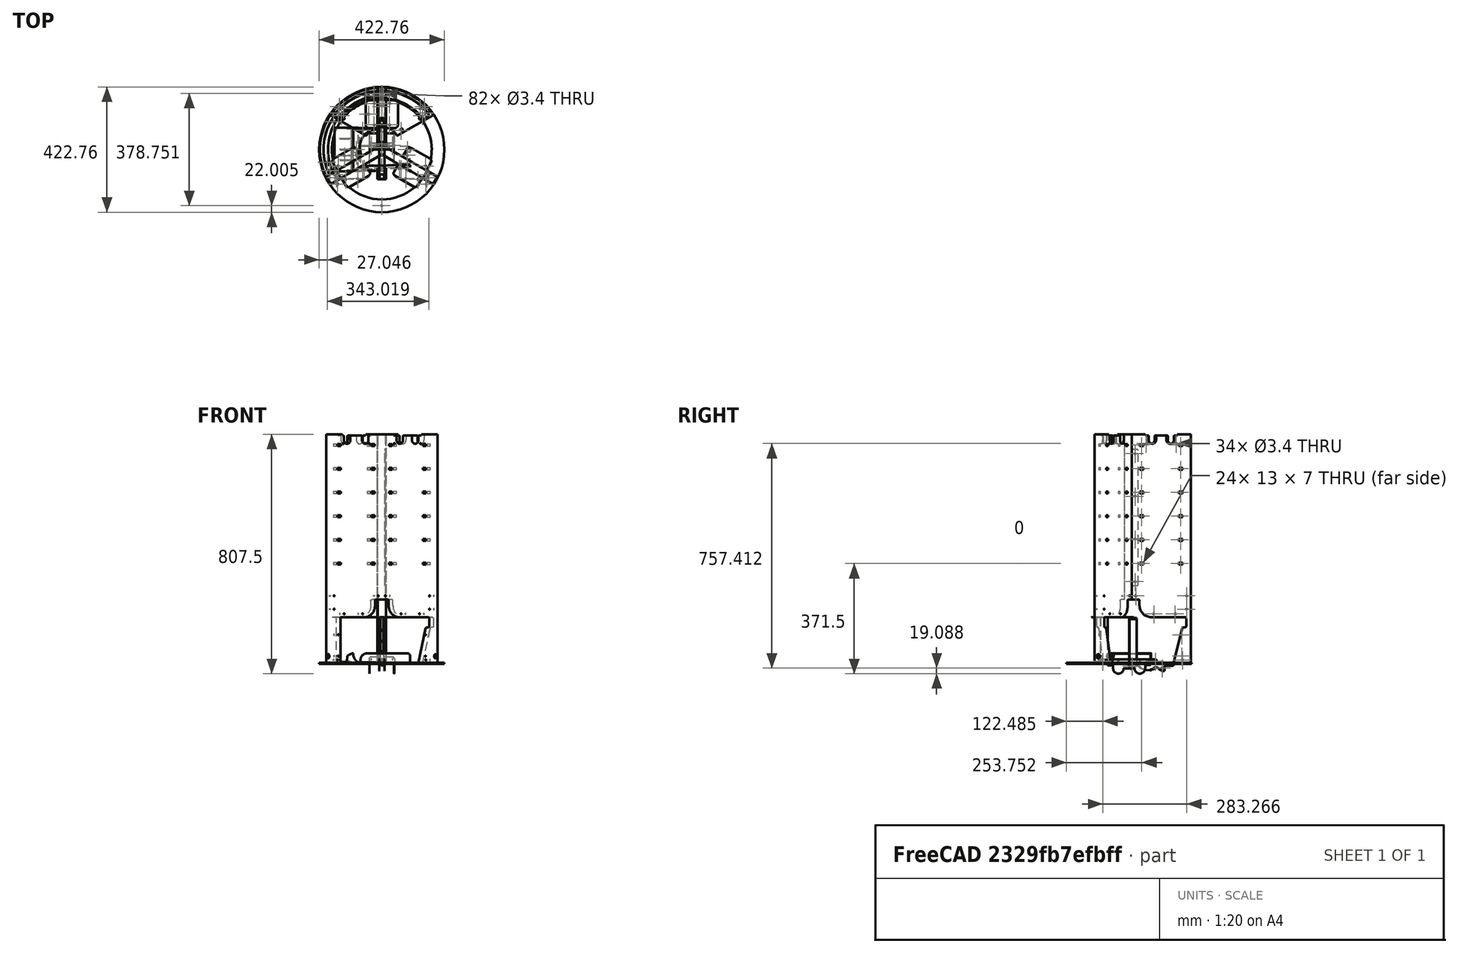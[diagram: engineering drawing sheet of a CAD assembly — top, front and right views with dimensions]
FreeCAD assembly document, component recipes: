
FREECAD ASSEMBLY — COMPONENT RECIPES ("composit_stand2_reserve")

This assembly document has 21 components, labeled P0..P20 below (a component is one placed body or linked part). 21 of them carry a construction recipe — the FreeCAD feature program that regenerates the part from scratch, quoted from this document or its linked companion documents; the rest are supplied as boundary geometry only. No exploded tour is included for this assembly.
NOTE — this tour is split across 2 documents so each fits a 32k-token context. This is document 1: the component sections continue in the remaining 1 document, each repeating the header above.
COMPONENT P0 — recipe-attached ("gutter001_material_0.50ansi", modeled in this document).
Construction recipe (the document's own serialized feature program — sketch geometry with constraints, then the solid features built on it; lengths are millimeters unless a unit is written):

FEATURE [Sketcher::SketchObject] Sketch  label="gutter_side_sketch"
  FullyConstrained = true
  MapMode = 5
  Support = -> [XY_Plane]
  sketch-geometry (15):
    g0: LineSegment StartX=0 StartY=150 StartZ=0 EndX=13.5 EndY=150 EndZ=0
    g1: LineSegment StartX=25.5 StartY=0 StartZ=0 EndX=0 EndY=0 EndZ=0
    g2: LineSegment StartX=15 StartY=148.5 StartZ=0 EndX=15 EndY=120 EndZ=0
    g3: LineSegment StartX=15 StartY=120 StartZ=0 EndX=29.7589 EndY=120 EndZ=0
    g4: GeomPoint X=25.5 Y=150 Z=0
    g5: ArcOfCircle CenterX=29.7589 CenterY=116.5 CenterZ=0 NormalX=0 NormalY=0 NormalZ=1 AngleXU=0 Radius=3.5 StartAngle=6.21662 EndAngle=7.85398
    g6: GeomPoint X=25.5 Y=0 Z=0
    g7: ArcOfCircle CenterX=13.5 CenterY=148.5 CenterZ=0 NormalX=0 NormalY=0 NormalZ=1 AngleXU=0 Radius=1.5 StartAngle=-2.7e-15 EndAngle=1.5708
    g8: GeomPoint X=15 Y=150 Z=0
    g9: LineSegment StartX=33.2511 StartY=116.267 StartZ=0 EndX=25.9178 EndY=6.26718 EndZ=0
    g10: LineSegment StartX=25.9178 StartY=6.26718 StartZ=0 EndX=25.5 EndY=0 EndZ=0
    g11: ArcOfCircle CenterX=22.4256 CenterY=6.5 CenterZ=0 NormalX=0 NormalY=0 NormalZ=1 AngleXU=0 Radius=3.5 StartAngle=4.71239 EndAngle=6.21662
    g12: LineSegment StartX=0 StartY=0 StartZ=0 EndX=0 EndY=3 EndZ=0
    g13: LineSegment StartX=0 StartY=3 StartZ=0 EndX=0 EndY=150 EndZ=0
    g14: LineSegment StartX=0 StartY=3 StartZ=0 EndX=22.4256 EndY=3 EndZ=0
  constraints (36):
    c: Coincident(g-1,g12)
    c: PointOnObject(g13,g-2)
    c: Coincident(g13,g0)
    c: Horizontal(g0)
    c: PointOnObject(g6,g-1)
    c: Coincident(g1,g12)
    c: Distance(g1,g6) = 25.5  'little_distance'
    c: Vertical(g2)
    c: Coincident(g3,g2)
    c: Horizontal(g3)
    c: DistanceY(g2,g8) = 30
    c: PointOnObject(g4,g0)
    c: Distance(g6,g4) = 150
    c: Distance(g0,g8) = 15
    c: Tangent(g3,g5) = 1.5708
    c: Diameter(g5) = 7
    c: PointOnObject(g8,g0)
    c: PointOnObject(g8,g2)
    c: Tangent(g0,g7) = 1.5708
    c: Tangent(g2,g7) = 1.5708
    c: Diameter(g7) = 3
    c: Tangent(g9,g5) = 1.5708
    c: Vertical(g4,g6)
    c: Coincident(g1,g6)
    c: Coincident(g10,g1)
    c: Coincident(g9,g10)
    c: Parallel(g9,g10)
    c: Angle(g10,g-1) = 1.63736
    c: Coincident(g12,g13)
    c: Vertical(g12)
    c: Coincident(g14,g12)
    c: Horizontal(g14)
    c: Tangent(g11,g9) = 1.5708
    c: Tangent(g14,g11) = -1.5708
    c: Equal(g11,g5)
    c: DistanceY(g12,g12) = 3
FEATURE [PartDesign::Pad] Pad  label="gutter_side_pad"
  Direction = (0,0,1)
  Length = 0.3
  Length2 = 10
  Profile = -> Sketch
  ReferenceAxis = -> Sketch [N_Axis]
  Type = 0
FEATURE [Sketcher::SketchObject] Sketch010
  FullyConstrained = true
  MapMode = 5
  Support = -> [XY_Plane]
  sketch-geometry (1):
    g0: LineSegment StartX=-8.49 StartY=0 StartZ=0 EndX=-8.49 EndY=150 EndZ=0
  constraints (4):
    c: PointOnObject(g0,g-1)
    c: Vertical(g0)
    c: DistanceX(g0) = -8.49
    c: DistanceY(g0) = 150
FEATURE [PartDesign::Mirrored] Mirrored005
  BaseFeature = -> Pad
  MirrorPlane = -> YZ_Plane
  Originals = -> [Pad]
  Refine = true
FEATURE [PartDesign::CoordinateSystem] Local_CS001
  AttacherType = Attacher::AttachEngine3D
  AttachmentOffset = pos=(-28.5,0,0) rot=(0,0,1;0.066568rad)
  MapMode = 5
  Placement = pos=(-28.5,0,0) rot=(0,0,1;0.066568rad)
  Support = -> [XY_Plane]
FEATURE [PartDesign::CoordinateSystem] Local_CS002
  AttacherType = Attacher::AttachEngine3D
  AttachmentOffset = pos=(28.5,0,0) rot=(0,0,1;-0.066568rad)
  MapMode = 5
  Placement = pos=(28.5,0,0) rot=(0,0,1;6.21662rad)
  Support = -> [XY_Plane]
FEATURE [PartDesign::CoordinateSystem] Local_CS003
  AttacherType = Attacher::AttachEngine3D
  AttachmentOffset = pos=(0,60,0) rot=(0,0,1;1.5708rad)
  MapMode = 5
  Placement = pos=(32.4911,59.8671,0) rot=(0,0,1;1.50423rad)
  Support = -> [Local_CS002]
FEATURE [PartDesign::CoordinateSystem] Local_CS004
  AttacherType = Attacher::AttachEngine3D
  AttachmentOffset = pos=(2,60,0) rot=(0,0,1;-1.5708rad)
  MapMode = 5
  Placement = pos=(-30.4956,60.0001,0) rot=(0,0,1;4.77896rad)
  Support = -> [Local_CS001]
FEATURE [PartDesign::Plane] DatumPlane003
  Length = 74.6163
  MapMode = 4
  Placement = pos=(32.4911,59.8671,0) rot=(0.023538,0.706911,0.706911;3.09453rad)
  ResizeMode = 0
  Support = -> [Local_CS003]
  Width = 61.2569
FEATURE [PartDesign::Plane] DatumPlane004
  Length = 72.6233
  MapMode = 4
  Placement = pos=(-30.4956,60.0001,0) rot=(0.998893,0.03326,0.03326;1.5719rad)
  ResizeMode = 0
  Support = -> [Local_CS004]
  Width = 61.0932
FEATURE [PartDesign::Plane] DatumPlane005
  AttachmentOffset = pos=(0,-1,0) rot=(0,0,1;0rad)
  Length = 199.341
  MapMode = 5
  Placement = pos=(33.4889,59.8006,0) rot=(0,0,1;1.50423rad)
  ResizeMode = 0
  Support = -> [Local_CS003]
  Width = 85.7622
FEATURE [PartDesign::Plane] DatumPlane006
  Length = 198.865
  MapMode = 5
  Placement = pos=(-30.4956,60.0001,0) rot=(0,0,-1;1.50423rad)
  ResizeMode = 0
  Support = -> [Local_CS004]
  Width = 82.4572
FEATURE [Sketcher::SketchObject] Sketch037
  AttachmentOffset = pos=(30,2,0) rot=(0,0,1;0rad)
  FullyConstrained = true
  MapMode = 5
  Placement = pos=(32.4911,89.9337,0) rot=(0,0,1;1.50423rad)
  Support = -> [Local_CS003]
  sketch-geometry (8):
    g0: LineSegment StartX=0 StartY=11.625 StartZ=0 EndX=1 EndY=11.625 EndZ=0
    g1: ArcOfCircle CenterX=1 CenterY=0 CenterZ=0 NormalX=0 NormalY=0 NormalZ=1 AngleXU=0 Radius=11.625 StartAngle=0.450911 EndAngle=1.5708
    g2: ArcOfCircle CenterX=17.127 CenterY=0 CenterZ=0 NormalX=0 NormalY=0 NormalZ=1 AngleXU=0 Radius=3 StartAngle=0.25268 EndAngle=1.29556
    g3: LineSegment StartX=12.0914 StartY=4.53943 StartZ=0 EndX=17.9423 EndY=2.88708 EndZ=0
    g4: LineSegment StartX=0 StartY=11.625 StartZ=0 EndX=0 EndY=0 EndZ=0
    g5: LineSegment StartX=0 StartY=0 StartZ=0 EndX=21 EndY=0 EndZ=0
    g6: ArcOfCircle CenterX=21 CenterY=1 CenterZ=0 NormalX=0 NormalY=0 NormalZ=1 AngleXU=0 Radius=1 StartAngle=3.39427 EndAngle=4.71239
    g7: ArcOfCircle CenterX=12.3631 CenterY=5.5018 CenterZ=0 NormalX=0 NormalY=0 NormalZ=1 AngleXU=0 Radius=1 StartAngle=3.5925 EndAngle=4.43715
  constraints (22):
    c: PointOnObject(g0,g-2)
    c: Horizontal(g0)
    c: PointOnObject(g2,g-1)
    c: Tangent(g3,g2) = 1.5708
    c: Tangent(g1,g0) = 1.5708
    c: Coincident(g4,g0)
    c: Coincident(g4,g-1)
    c: Coincident(g5,g4)
    c: Diameter(g2) = 6
    c: Angle(g3,g-1) = 0.275238
    c: Diameter(g1) = 23.25
    c: PointOnObject(g1,g-1)
    c: Distance(g0) = 1
    c: Horizontal(g5)
    c: Tangent(g6,g5) = -1.5708
    c: Tangent(g6,g2) = 1.5708
    c: Diameter(g6) = 2
    c: Distance(g5) = 21
    c: Tangent(g3,g7) = -1.5708
    c: Tangent(g1,g7) = 1.5708
    c: Diameter(g7) = 2
    c: DistanceY(g2) = 2.88708  'arc_height'
FEATURE [PartDesign::Pocket] Pocket008
  BaseFeature = -> Mirrored005
  Direction = (0,0,-1)
  Length = 5
  Length2 = 5
  Midplane = true
  Profile = -> Sketch037
  ReferenceAxis = -> Sketch037 [N_Axis]
  Type = 1
FEATURE [PartDesign::Mirrored] Mirrored006
  MirrorPlane = -> Sketch037 [V_Axis]
FEATURE [PartDesign::Mirrored] Mirrored007
  MirrorPlane = -> DatumPlane003
FEATURE [PartDesign::MultiTransform] MultiTransform002
  BaseFeature = -> Pocket008
  Originals = -> [Pocket008]
  Transformations = -> [Mirrored006,Mirrored007]
FEATURE [PartDesign::SubShapeBinder] Binder
  AttacherType = Attacher::AttachEngine3D
  AttachmentOffset = pos=(35,0,0) rot=(0,0,1;0rad)
  BindCopyOnChange = 0
  BindMode = 0
  ClaimChildren = true
  Context = -> Body [Binder.]
  Fuse = false
  MakeFace = true
  MapMode = 5
  OffsetFill = false
  OffsetIntersection = false
  OffsetJoinType = 0
  OffsetOpenResult = false
  PartialLoad = false
  Placement = pos=(-28.1674,25.0777,0) rot=(0,0,-1;1.50423rad)
  Relative = false
  _Version = 2
FEATURE [PartDesign::Pocket] Pocket009
  BaseFeature = -> MultiTransform002
  Direction = (0,0,-1)
  Length = 5
  Length2 = 5
  Midplane = true
  Profile = -> Binder
  Type = 1
FEATURE [PartDesign::Plane] DatumPlane007
  Length = 72.6233
  MapMode = 4
  Placement = pos=(-28.1674,25.0777,0) rot=(0.998893,0.03326,0.03326;1.5719rad)
  ResizeMode = 0
  Support = -> [Binder]
  Width = 61.0932
FEATURE [PartDesign::Mirrored] Mirrored008
  MirrorPlane = -> DatumPlane007
FEATURE [PartDesign::Mirrored] Mirrored009
  MirrorPlane = -> DatumPlane004
FEATURE [PartDesign::MultiTransform] MultiTransform003
  BaseFeature = -> Pocket009
  Originals = -> [Pocket009]
  Transformations = -> [Mirrored008,Mirrored009]
FEATURE [Sketcher::SketchObject] Sketch038
  FullyConstrained = true
  MapMode = 5
  Support = -> [XY_Plane]
  sketch-geometry (1):
    g0: LineSegment StartX=8.49 StartY=0 StartZ=0 EndX=8.49 EndY=150 EndZ=0
  constraints (4):
    c: PointOnObject(g0,g-1)
    c: Vertical(g0)
    c: DistanceX(g0) = 8.49
    c: DistanceY(g0) = 150
FEATURE [Sketcher::SketchObject] Sketch039
  AttachmentOffset = pos=(51,14,0) rot=(0,0,1;0rad)
  FullyConstrained = true
  MapMode = 5
  Placement = pos=(22.9124,111.619,0) rot=(0,0,1;1.50423rad)
  Support = -> [DatumPlane005]
  sketch-geometry (1):
    g0: Circle CenterX=0 CenterY=0 CenterZ=0 NormalX=0 NormalY=0 NormalZ=1 AngleXU=0 Radius=1.7
  constraints (2):
    c: Coincident(g0,g-1)
    c: Diameter(g0) = 3.4
FEATURE [PartDesign::Pocket] Pocket010
  BaseFeature = -> MultiTransform003
  Direction = (0,0,-1)
  Length = 5
  Length2 = 5
  Midplane = true
  Profile = -> Sketch039
  ReferenceAxis = -> Sketch039 [N_Axis]
  Type = 1
FEATURE [PartDesign::Mirrored] Mirrored010
  MirrorPlane = -> DatumPlane003
FEATURE [PartDesign::Mirrored] Mirrored011
  MirrorPlane = -> YZ_Plane
FEATURE [PartDesign::MultiTransform] MultiTransform004
  BaseFeature = -> Pocket010
  Originals = -> [Pocket010]
  Transformations = -> [Mirrored010,Mirrored011]
FEATURE [PartDesign::FeaturePython] Fold  # WARN: FeaturePython — macro-defined, semantics opaque (R4)
  BaseFeature = -> MultiTransform004
  BendLine = -> Sketch038
  Position = 0
  angle = 90
  baseObject = -> MultiTransform004 [Face4]
  invert = false
  invertbend = true
  kfactor = 0.01
  radius = 0.01
  unfold = false
FEATURE [PartDesign::FeaturePython] Fold002  # WARN: FeaturePython — macro-defined, semantics opaque (R4)
  BaseFeature = -> Fold
  BendLine = -> Sketch010
  Position = 0
  angle = 90
  baseObject = -> Fold [Face2]
  invert = false
  invertbend = false
  kfactor = 0.01
  radius = 0.01
  unfold = false
FEATURE [PartDesign::CoordinateSystem] Local_CS024
  AttacherType = Attacher::AttachEngine3D
  AttachmentOffset = pos=(0,60,-10.3215) rot=(-1,0,0;0.066568rad)
  MapMode = 5
  Placement = pos=(0,60,-10.3215) rot=(-1,0,0;0.066568rad)
  Support = -> [XY_Plane]
FEATURE [Sketcher::SketchObject] Sketch115
  FullyConstrained = true
  MapMode = 5
  Support = -> [XY_Plane]
  sketch-geometry (1):
    g0: Circle CenterX=0 CenterY=145 CenterZ=0 NormalX=0 NormalY=0 NormalZ=1 AngleXU=0 Radius=1.7
  constraints (3):
    c: PointOnObject(g0,g-2)
    c: Diameter(g0) = 3.4
    c: DistanceY(g0) = 145
FEATURE [PartDesign::Pocket] Pocket070
  BaseFeature = -> Fold002
  Direction = (0,0,-1)
  Length = 5
  Length2 = 5
  Midplane = true
  Profile = -> Sketch115
  ReferenceAxis = -> Sketch115 [N_Axis]
  Type = 1
FEATURE [PartDesign::Body] Body  label="gutter001_material_0.50ansi"
  Group = -> [Sketch,Pad,Mirrored005,Local_CS001,Local_CS002,Local_CS003,Local_CS004,DatumPlane003,DatumPlane004,DatumPlane005,DatumPlane006,Sketch037,Pocket008,MultiTransform002,Mirrored006,Mirrored007,Binder,Pocket009,MultiTransform003,Mirrored008,DatumPlane007,Mirrored009,Sketch010,Sketch038,Sketch039,Pocket010,MultiTransform004,Mirrored010,Mirrored011,Fold,Fold002,Local_CS024,Sketch115,Pocket070]
  Origin = -> Origin
  Tip = -> Pocket070
COMPONENT P1 — recipe-attached ("Body001_material_0.30ansi", modeled in this document).
Construction recipe (the document's own serialized feature program — sketch geometry with constraints, then the solid features built on it; lengths are millimeters unless a unit is written):

FEATURE [Sketcher::SketchObject] Sketch003
  FullyConstrained = true
  MapMode = 5
  Support = -> [XY_Plane001]
  sketch-geometry (12):
    g0: LineSegment StartX=-14.5 StartY=8.37158 StartZ=0 EndX=-14.5 EndY=208.372 EndZ=0
    g1: LineSegment StartX=-14.5 StartY=208.372 StartZ=0 EndX=14.5 EndY=208.372 EndZ=0
    g2: LineSegment StartX=14.5 StartY=208.372 StartZ=0 EndX=14.5 EndY=8.37158 EndZ=0
    g3: LineSegment StartX=14.5 StartY=8.37158 StartZ=0 EndX=187.705 EndY=-91.6284 EndZ=0
    g4: LineSegment StartX=187.705 StartY=-91.6284 StartZ=0 EndX=173.205 EndY=-116.743 EndZ=0
    g5: LineSegment StartX=173.205 StartY=-116.743 StartZ=0 EndX=0 EndY=-16.7432 EndZ=0
    g6: LineSegment StartX=0 StartY=-16.7432 StartZ=0 EndX=-173.205 EndY=-116.743 EndZ=0
    g7: LineSegment StartX=-173.205 StartY=-116.743 StartZ=0 EndX=-187.705 EndY=-91.6284 EndZ=0
    g8: LineSegment StartX=-187.705 StartY=-91.6284 StartZ=0 EndX=-14.5 EndY=8.37158 EndZ=0
    g9: LineSegment StartX=-14.5 StartY=8.37158 StartZ=0 EndX=0 EndY=0 EndZ=0
    g10: LineSegment StartX=0 StartY=0 StartZ=0 EndX=14.5 EndY=8.37158 EndZ=0
    g11: LineSegment StartX=0 StartY=0 StartZ=0 EndX=0 EndY=-16.7432 EndZ=0
  constraints (39):
    c: Vertical(g0)
    c: Coincident(g0,g1)
    c: Horizontal(g1)
    c: Coincident(g1,g2)
    c: Vertical(g2)
    c: Coincident(g2,g3)
    c: Coincident(g3,g4)
    c: Coincident(g4,g5)
    c: PointOnObject(g5,g-2)
    c: Coincident(g5,g6)
    c: Coincident(g6,g7)
    c: Coincident(g8,g7)
    c: Equal(g2,g6)
    c: Equal(g6,g5)
    c: Equal(g5,g3)
    c: Equal(g4,g7)
    c: Equal(g7,g1)
    c: Perpendicular(g4,g5)
    c: Perpendicular(g4,g3)
    c: Perpendicular(g7,g6)
    c: Perpendicular(g8,g7)
    c: Angle(g6,g5) = 2.0944
    c: Angle(g3,g2) = 2.0944
    c: Coincident(g9,g0)
    c: Coincident(g9,g-1)
    c: Coincident(g10,g9)
    c: Coincident(g10,g2)
    c: Coincident(g11,g9)
    c: Coincident(g11,g5)
    c: Equal(g10,g11)
    c: DistanceX(g1,g1) = 29
    c: DistanceY(g2,g2) = 200
    c: DistanceY(g9,g2) = 8.37158  'petal_offset'
    c: DistanceY(g0) = 8.37158  'petal_conn_y'
    c: Coincident(g8,g0)
    c: DistanceX(g2) = 14.5  'petal_conn_x'
    c: Distance(g9,g1) = 208.875  'max_r'
    c: Distance(g10) = 16.7432  'planes_intersec_r'
    c: DistanceY(g9,g1) = 208.372  'total_petal_length'
FEATURE [PartDesign::FeaturePython] BaseBend001  # WARN: FeaturePython — macro-defined, semantics opaque (R4)
  BendSide = 0
  BendSketch = -> Sketch003
  MidPlane = false
  Reverse = false
  length = 774
  radius = 0.01
  thickness = 0.3
FEATURE [PartDesign::CoordinateSystem] Local_CS
  AttacherType = Attacher::AttachEngine3D
  AttachmentOffset = pos=(0,8.37158,0) rot=(0,0,1;0rad)
  MapMode = 5
  Placement = pos=(0,8.37158,0) rot=(0,0,1;0rad)
  Support = -> [XY_Plane001]
FEATURE [PartDesign::Pocket] Pocket001
  BaseFeature = -> BaseBend001
  Direction = (0,0,-1)
  Length = 5
  Length2 = 5
  Midplane = true
  Profile = -> Sketch005
  ReferenceAxis = -> Sketch005 [N_Axis]
  Type = 1
FEATURE [PartDesign::FeaturePython] Bend009  # WARN: FeaturePython — macro-defined, semantics opaque (R4)
  AutoMiter = true
  BaseFeature = -> Pocket001
  BendType = 1
  LengthList = [203.464]
  LengthSpec = 0
  ReliefFactor = 0.7
  UseReliefFactor = false
  angle = 90
  baseObject = -> Pocket001 [Face61]
  bendAList = [90]
  extend1 = 0
  extend2 = 0
  gap1 = 0
  gap2 = 0
  invert = false
  kfactor = 0.5
  length = 203.464
  maxExtendDist = 5
  minGap = 0.1
  minReliefGap = 1
  miterangle1 = 0
  miterangle2 = 0
  offset = 0
  radius = 0.01
  reliefType = 0
  reliefd = 1
  reliefw = 0.8
  sketchflip = false
  sketchinvert = false
  unfold = false
FEATURE [PartDesign::FeaturePython] Bend010  # WARN: FeaturePython — macro-defined, semantics opaque (R4)
  AutoMiter = true
  BaseFeature = -> Bend009
  BendType = 0
  LengthList = [20]
  LengthSpec = 0
  ReliefFactor = 0.7
  UseReliefFactor = false
  angle = 60
  baseObject = -> Bend009 [Face3]
  bendAList = [60]
  extend1 = 0
  extend2 = 0
  gap1 = 0
  gap2 = 0
  invert = true
  kfactor = 0.5
  length = 20
  maxExtendDist = 5
  minGap = 0.1
  minReliefGap = 1
  miterangle1 = 0
  miterangle2 = 0
  offset = 0
  radius = 0.01
  reliefType = 0
  reliefd = 1
  reliefw = 0.8
  sketchflip = false
  sketchinvert = false
  unfold = false
FEATURE [PartDesign::CoordinateSystem] Local_CS011
  AttacherType = Attacher::AttachEngine3D
  AttachmentOffset = pos=(0,100,0) rot=(0,0,1;0rad)
  MapMode = 5
  Placement = pos=(0,108.372,0) rot=(0,0,1;0rad)
  Support = -> [Local_CS]
FEATURE [PartDesign::Plane] DatumPlane011
  AttachmentOffset = pos=(0,0,0) rot=(0,0,1;0.523599rad)
  Length = 589.355
  MapMode = 5
  Placement = pos=(0,0,0) rot=(0,0,1;0.523599rad)
  ResizeMode = 0
  Support = -> [XY_Plane001]
  Width = 574.61
FEATURE [PartDesign::CoordinateSystem] Local_CS035
  AttacherType = Attacher::AttachEngine3D
  AttachmentOffset = pos=(0,0,774) rot=(0,0,1;0rad)
  MapMode = 5
  Placement = pos=(0,108.372,774) rot=(0,0,1;0rad)
  Support = -> [Local_CS011]
FEATURE [PartDesign::CoordinateSystem] Local_CS036  label="droppers_center"
  AttacherType = Attacher::AttachEngine3D
  AttachmentOffset = pos=(0,0,-19) rot=(0,0,1;0rad)
  MapMode = 5
  Placement = pos=(0,108.372,755) rot=(0,0,1;0rad)
  Support = -> [Local_CS035]
FEATURE [PartDesign::CoordinateSystem] Local_CS037  label="gutter_fixture_center"
  AttacherType = Attacher::AttachEngine3D
  AttachmentOffset = pos=(0,0,-12) rot=(0,0,1;0rad)
  MapMode = 5
  Placement = pos=(0,108.372,743) rot=(0,0,1;0rad)
  Support = -> [Local_CS036]
FEATURE [PartDesign::CoordinateSystem] Local_CS038  label="modules_top_center"
  AttacherType = Attacher::AttachEngine3D
  AttachmentOffset = pos=(0,0,-5) rot=(0,0,1;0rad)
  MapMode = 5
  Placement = pos=(0,108.372,738) rot=(0,0,1;0rad)
  Support = -> [Local_CS037]
FEATURE [Sketcher::SketchObject] Sketch112
  FullyConstrained = true
  MapMode = 5
  Placement = pos=(0,0,0) rot=(0.57735,0.57735,0.57735;2.0944rad)
  Support = -> [YZ_Plane001]
  sketch-geometry (5):
    g0: LineSegment StartX=-6.5 StartY=-3.5 StartZ=0 EndX=-6.5 EndY=3.5 EndZ=0
    g1: LineSegment StartX=-6.5 StartY=3.5 StartZ=0 EndX=6.5 EndY=3.5 EndZ=0
    g2: LineSegment StartX=6.5 StartY=3.5 StartZ=0 EndX=6.5 EndY=-3.5 EndZ=0
    g3: LineSegment StartX=6.5 StartY=-3.5 StartZ=0 EndX=-6.5 EndY=-3.5 EndZ=0
    g4: GeomPoint X=0 Y=0 Z=0
  constraints (12):
    c: Coincident(g0,g1)
    c: Coincident(g1,g2)
    c: Coincident(g2,g3)
    c: Coincident(g3,g0)
    c: Horizontal(g1)
    c: Horizontal(g3)
    c: Vertical(g0)
    c: Vertical(g2)
    c: Symmetric(g1,g0,g4)
    c: Coincident(g4,g-1)
    c: DistanceX(g1,g1) = 13
    c: DistanceY(g2,g2) = 7
FEATURE [Sketcher::SketchObject] Sketch113
  FullyConstrained = true
  MapMode = 5
  Placement = pos=(0,0,0) rot=(0.57735,0.57735,0.57735;2.0944rad)
  Support = -> [YZ_Plane001]
  sketch-geometry (8):
    g0: ArcOfCircle CenterX=0 CenterY=0 CenterZ=0 NormalX=0 NormalY=0 NormalZ=1 AngleXU=0 Radius=12.625 StartAngle=3.14159 EndAngle=6.28319
    g1: LineSegment StartX=12.625 StartY=-3.1e-15 StartZ=0 EndX=12.625 EndY=12.5 EndZ=0
    g2: LineSegment StartX=-12.625 StartY=1.5e-15 StartZ=0 EndX=-12.625 EndY=12.5 EndZ=0
    g3: ArcOfCircle CenterX=15.125 CenterY=12.5 CenterZ=0 NormalX=0 NormalY=0 NormalZ=1 AngleXU=0 Radius=2.5 StartAngle=1.5708 EndAngle=3.14159
    g4: ArcOfCircle CenterX=-15.125 CenterY=12.5 CenterZ=0 NormalX=0 NormalY=0 NormalZ=1 AngleXU=0 Radius=2.5 StartAngle=0 EndAngle=1.5708
    g5: LineSegment StartX=-15.125 StartY=15 StartZ=0 EndX=-15.125 EndY=19 EndZ=0
    g6: LineSegment StartX=-15.125 StartY=19 StartZ=0 EndX=15.125 EndY=19 EndZ=0
    g7: LineSegment StartX=15.125 StartY=19 StartZ=0 EndX=15.125 EndY=15 EndZ=0
  constraints (24):
    c: Coincident(g0,g-1)
    c: PointOnObject(g0,g-1)
    c: PointOnObject(g0,g-1)
    c: Coincident(g1,g0)
    c: Vertical(g1)
    c: Coincident(g2,g0)
    c: Vertical(g2)
    c: Coincident(g5,g4)
    c: Vertical(g5)
    c: Coincident(g6,g5)
    c: Horizontal(g6)
    c: Coincident(g7,g6)
    c: Coincident(g7,g3)
    c: Vertical(g7)
    c: Perpendicular(g3,g7)
    c: Tangent(g3,g1) = 1.5708
    c: Tangent(g4,g2) = -1.5708
    c: Perpendicular(g4,g5)
    c: Diameter(g0) = 25.25
    c: Distance(g0,g6) = 19
    c: Equal(g4,g3)
    c: Diameter(g4) = 5
    c: DistanceY(g7,g7) = 4
    c: Equal(g5,g7)
FEATURE [PartDesign::CoordinateSystem] Local_CS039
  AttacherType = Attacher::AttachEngine3D
  AttachmentOffset = pos=(119.5,154,11.5) rot=(0,0.707107,0.707107;3.14159rad)
  MapMode = 5
  Placement = pos=(11.5,119.5,154) rot=(0,0,1;4.71239rad)
  Support = -> [YZ_Plane001]
FEATURE [Sketcher::SketchObject] Sketch128
  FullyConstrained = true
  MapMode = 5
  Placement = pos=(0,0,0) rot=(0.57735,0.57735,0.57735;2.0944rad)
  Support = -> [YZ_Plane001]
  sketch-geometry (4):
    g0: LineSegment StartX=73 StartY=116.5 StartZ=0 EndX=166 EndY=116.5 EndZ=0
    g1: LineSegment StartX=166 StartY=116.5 StartZ=0 EndX=166 EndY=157 EndZ=0
    g2: LineSegment StartX=166 StartY=157 StartZ=0 EndX=73 EndY=157 EndZ=0
    g3: LineSegment StartX=73 StartY=157 StartZ=0 EndX=73 EndY=116.5 EndZ=0
  constraints (12):
    c: Coincident(g0,g1)
    c: Coincident(g1,g2)
    c: Coincident(g2,g3)
    c: Coincident(g3,g0)
    c: Horizontal(g0)
    c: Horizontal(g2)
    c: Vertical(g1)
    c: Vertical(g3)
    c: DistanceX(g0,g0) = 93  'length'
    c: DistanceY(g3,g3) = 40.5  'height'
    c: DistanceX(g0) = 73  'offset_x'
    c: DistanceY(g2) = 157
FEATURE [PartDesign::Pocket] Pocket081
  BaseFeature = -> Bend010
  Direction = (-1,2e-16,-3e-16)
  Length = 5
  Length2 = 5
  Midplane = true
  Profile = -> Sketch128
  ReferenceAxis = -> Sketch128 [N_Axis]
  Type = 1
FEATURE [PartDesign::PolarPattern] PolarPattern016
  Angle = 360
  Axis = -> Z_Axis001
  BaseFeature = -> Pocket081
  Occurrences = 3
  Originals = -> [Pocket081]
FEATURE [PartDesign::FeaturePython] Bend  # WARN: FeaturePython — macro-defined, semantics opaque (R4)
  AutoMiter = true
  BaseFeature = -> PolarPattern016
  BendType = 0
  LengthList = [40]
  LengthSpec = 2
  ReliefFactor = 0.7
  UseReliefFactor = false
  angle = 90
  baseObject = -> PolarPattern016 [Edge222,Edge178,Edge34,Edge78,Edge106,Edge150]
  bendAList = [90]
  extend1 = 0
  extend2 = 0
  gap1 = 0.1
  gap2 = 0.1
  invert = false
  kfactor = 0.5
  length = 40
  maxExtendDist = 5
  minGap = 0.1
  minReliefGap = 1
  miterangle1 = 0
  miterangle2 = 0
  offset = 0
  radius = 0.1
  reliefType = 0
  reliefd = 1
  reliefw = 0.8
  sketchflip = false
  sketchinvert = false
  unfold = false
FEATURE [Sketcher::SketchObject] Sketch129
  AttachmentOffset = pos=(0,0,0) rot=(0,1,0;3.66519rad)
  FullyConstrained = true
  MapMode = 5
  Placement = pos=(0,0,0) rot=(-0.186157,0.694747,0.694747;3.50969rad)
  Support = -> [XZ_Plane001]
  sketch-geometry (9):
    g0: LineSegment StartX=0 StartY=0 StartZ=0 EndX=169.18 EndY=0 EndZ=0
    g1: LineSegment StartX=169.18 StartY=0 StartZ=0 EndX=169.18 EndY=157 EndZ=0
    g2: LineSegment StartX=0 StartY=157 StartZ=0 EndX=0 EndY=0 EndZ=0
    g3: LineSegment StartX=73 StartY=116.5 StartZ=0 EndX=166 EndY=116.5 EndZ=0
    g4: LineSegment StartX=166 StartY=116.5 StartZ=0 EndX=166 EndY=157 EndZ=0
    g5: LineSegment StartX=166 StartY=157 StartZ=0 EndX=73 EndY=157 EndZ=0
    g6: LineSegment StartX=73 StartY=157 StartZ=0 EndX=73 EndY=116.5 EndZ=0
    g7: LineSegment StartX=169.18 StartY=157 StartZ=0 EndX=166 EndY=157 EndZ=0
    g8: LineSegment StartX=73 StartY=157 StartZ=0 EndX=0 EndY=157 EndZ=0
  constraints (25):
    c: Coincident(g0,g1)
    c: Coincident(g1,g7)
    c: Coincident(g8,g2)
    c: Coincident(g2,g0)
    c: Horizontal(g0)
    c: Vertical(g1)
    c: Vertical(g2)
    c: Coincident(g0,g-1)
    c: DistanceY(g8) = 157
    c: Coincident(g3,g4)
    c: Coincident(g4,g5)
    c: Coincident(g5,g6)
    c: Coincident(g6,g3)
    c: Horizontal(g3)
    c: Horizontal(g5)
    c: Vertical(g4)
    c: Vertical(g6)
    c: DistanceX(g3,g3) = 93  'length'
    c: DistanceY(g6,g6) = 40.5  'height'
    c: DistanceX(g3) = 73
    c: DistanceY(g5) = 157
    c: Horizontal(g7)
    c: Coincident(g8,g5)
    c: Coincident(g7,g4)
    c: DistanceX(g7,g7) = 3.18
FEATURE [PartDesign::CoordinateSystem] Local_CS041
  AttacherType = Attacher::AttachEngine3D
  AttachmentOffset = pos=(119.5,157,14.5) rot=(0,0.707107,0.707107;3.14159rad)
  MapMode = 5
  Placement = pos=(14.5,119.5,157) rot=(0,0,1;4.71239rad)
  Support = -> [YZ_Plane001]
FEATURE [Sketcher::SketchObject] Sketch130
  AttachmentOffset = pos=(0,40,0) rot=(0,0,1;0rad)
  FullyConstrained = true
  MapMode = 5
  Placement = pos=(54.5,119.5,157) rot=(0,0,-1;1.5708rad)
  Support = -> [Local_CS041]
  sketch-geometry (6):
    g0: ArcOfCircle CenterX=36.5 CenterY=-10 CenterZ=0 NormalX=0 NormalY=0 NormalZ=1 AngleXU=0 Radius=10 StartAngle=6.28318 EndAngle=7.85398
    g1: ArcOfCircle CenterX=-36.5 CenterY=-10 CenterZ=0 NormalX=0 NormalY=0 NormalZ=1 AngleXU=0 Radius=10 StartAngle=1.5708 EndAngle=3.14159
    g2: LineSegment StartX=-46.5 StartY=-10 StartZ=0 EndX=-46.5 EndY=0 EndZ=0
    g3: LineSegment StartX=-36.5 StartY=0 StartZ=0 EndX=-46.5 EndY=0 EndZ=0
    g4: LineSegment StartX=46.5 StartY=-10 StartZ=0 EndX=46.5 EndY=0 EndZ=0
    g5: LineSegment StartX=36.5 StartY=0 StartZ=0 EndX=46.5 EndY=0 EndZ=0
  constraints (17):
    c: PointOnObject(g0,g-1)
    c: PointOnObject(g1,g-1)
    c: Coincident(g2,g1)
    c: PointOnObject(g2,g-1)
    c: Vertical(g2)
    c: Tangent(g2,g1)
    c: Coincident(g3,g2)
    c: Coincident(g4,g0)
    c: PointOnObject(g4,g-1)
    c: Vertical(g4)
    c: Tangent(g4,g0)
    c: Coincident(g5,g4)
    c: Tangent(g5,g0) = 1.5708
    c: Tangent(g3,g1) = -1.5708
    c: DistanceX(g2,g4) = 93
    c: Symmetric(g1,g0,g-2)
    c: Diameter(g0) = 20
FEATURE [PartDesign::Pocket] Pocket083
  BaseFeature = -> Bend
  Direction = (0,-3e-16,-1)
  Length = 5
  Length2 = 5
  Midplane = true
  Profile = -> Sketch130
  ReferenceAxis = -> Sketch130 [N_Axis]
  Type = 1
FEATURE [PartDesign::Mirrored] Mirrored040
  MirrorPlane = -> YZ_Plane001
FEATURE [PartDesign::PolarPattern] PolarPattern017
  Angle = 360
  Axis = -> Z_Axis001
  Occurrences = 3
FEATURE [PartDesign::MultiTransform] MultiTransform014
  BaseFeature = -> Pocket083
  Originals = -> [Pocket083]
  Transformations = -> [Mirrored040,PolarPattern017]
FEATURE [PartDesign::Pocket] Pocket082
  BaseFeature = -> MultiTransform014
  Direction = (0.5,-0.866025,-1e-16)
  Length = 30
  Length2 = 5
  Midplane = true
  Profile = -> Sketch129
  ReferenceAxis = -> Sketch129 [N_Axis]
  Type = 0
FEATURE [PartDesign::Pocket] Pocket006
  BaseFeature = -> Pocket082
  Direction = (-1,2e-16,-3e-16)
  Length = 30
  Length2 = 160
  Midplane = true
  Profile = -> Sketch009
  ReferenceAxis = -> Sketch009 [N_Axis]
  Type = 0
FEATURE [PartDesign::Mirrored] Mirrored002
  BaseFeature = -> Pocket006
  MirrorPlane = -> DatumPlane014
  Originals = -> [Pocket006]
FEATURE [PartDesign::Pocket] Pocket014
  BaseFeature = -> Mirrored002
  Direction = (-1,2e-16,-3e-16)
  Length = 5
  Length2 = 5
  Midplane = true
  Profile = -> Sketch013
  ReferenceAxis = -> Sketch013 [N_Axis]
  Type = 1
FEATURE [PartDesign::PolarPattern] PolarPattern003
  Angle = 360
  Axis = -> Z_Axis001
  BaseFeature = -> Pocket014
  Occurrences = 3
  Originals = -> [Pocket014]
  Refine = true
FEATURE [PartDesign::Pocket] Pocket007
  BaseFeature = -> PolarPattern003
  Direction = (-1,2e-16,-3e-16)
  Length = 11.5
  Length2 = 5
  Profile = -> Sketch012
  ReferenceAxis = -> Sketch012 [N_Axis]
  Reversed = true
  Type = 0
FEATURE [PartDesign::CoordinateSystem] Local_CS042
  AttacherType = Attacher::AttachEngine3D
  AttachmentOffset = pos=(0,0,0) rot=(0,0,1;2.0944rad)
  MapMode = 5
  Placement = pos=(0,0,0) rot=(0,0,1;2.0944rad)
  Support = -> [XY_Plane001]
FEATURE [PartDesign::CoordinateSystem] Local_CS012
  AttacherType = Attacher::AttachEngine3D
  AttachmentOffset = pos=(14.5,119.5,157) rot=(0,0,1;4.71239rad)
  MapMode = 5
  Placement = pos=(-110.74,-47.1926,157) rot=(0,0,-1;5.75959rad)
  Support = -> [Local_CS042]
FEATURE [PartDesign::Plane] DatumPlane012
  Length = 589.355
  MapMode = 5
  Placement = pos=(-110.74,-47.1926,157) rot=(0,0,1;0.523599rad)
  ResizeMode = 0
  Support = -> [Local_CS012]
  Width = 574.61
FEATURE [PartDesign::Body] Body001  label="Body001_material_0.30ansi"
  Group = -> [Local_CS,Local_CS011,Sketch003,BaseBend001,Local_CS012,DatumPlane011,DatumPlane012,Local_CS035,Local_CS036,Local_CS037,Local_CS038,Sketch112,Sketch113,Pocket001,Bend009,Bend010,Sketch128,Pocket081,Local_CS039,PolarPattern016,Bend,Sketch129,Local_CS041,Sketch130,Pocket083,MultiTransform014,Mirrored040,PolarPattern017,Local_CS042,Pocket082,Pocket006,Mirrored002,Pocket014,PolarPattern003,Pocket007,+64 more]
  Origin = -> Origin001
  Tip = -> MultiTransform012
COMPONENT P2 — recipe-attached ("module001", modeled in this document).
Construction recipe (the document's own serialized feature program — sketch geometry with constraints, then the solid features built on it; lengths are millimeters unless a unit is written):

FEATURE [PartDesign::FeatureBase] BaseFeature
  BaseFeature = -> Part__Feature
FEATURE [PartDesign::CoordinateSystem] Local_CS009
  AttacherType = Attacher::AttachEngine3D
  MapMode = 45
  Placement = pos=(0,0,0) rot=(0,0.707107,0.707107;3.14159rad)
  Support = -> [BaseFeature]
FEATURE [PartDesign::Body] Body001003  label="module001"
  BaseFeature = -> Part__Feature
  Group = -> [BaseFeature,Local_CS009]
  Origin = -> Origin013
  Tip = -> BaseFeature
COMPONENT P3 — recipe-attached ("basin_cover", modeled in this document).
Construction recipe (the document's own serialized feature program — sketch geometry with constraints, then the solid features built on it; lengths are millimeters unless a unit is written):

FEATURE [Sketcher::SketchObject] Sketch047
  FullyConstrained = true
  MapMode = 5
  Support = -> [XY_Plane015]
  sketch-geometry (8):
    g0: ArcOfCircle CenterX=0 CenterY=16.7432 CenterZ=0 NormalX=0 NormalY=0 NormalZ=1 AngleXU=0 Radius=60 StartAngle=0.539993 EndAngle=1.5708
    g1: ArcOfCircle CenterX=52.3205 CenterY=48.1051 CenterZ=0 NormalX=0 NormalY=0 NormalZ=1 AngleXU=0 Radius=1 StartAngle=3.68159 EndAngle=5.23599
    g2: LineSegment StartX=52.8205 StartY=47.2391 StartZ=0 EndX=172.274 EndY=116.206 EndZ=0
    g3: ArcOfCircle CenterX=171.774 CenterY=117.072 CenterZ=0 NormalX=0 NormalY=0 NormalZ=1 AngleXU=0 Radius=1 StartAngle=5.23599 EndAngle=6.88142
    g4: ArcOfCircle CenterX=0 CenterY=0 CenterZ=0 NormalX=0 NormalY=0 NormalZ=1 AngleXU=0 Radius=208.875 StartAngle=0.598232 EndAngle=1.5708
    g5: LineSegment StartX=3.7e-15 StartY=76.7432 StartZ=0 EndX=1.28e-14 EndY=208.875 EndZ=0
    g6: LineSegment StartX=52.8205 StartY=47.2391 StartZ=0 EndX=0 EndY=16.7432 EndZ=0
    g7: GeomPoint X=173.205 Y=116.743 Z=0
  constraints (22):
    c: PointOnObject(g0,g-2)
    c: PointOnObject(g4,g-2)
    c: Diameter(g1) = 2
    c: Diameter(g3) = 2
    c: Tangent(g1,g0) = 1.5708
    c: Tangent(g3,g2) = -1.5708
    c: Angle(g2,g-1) = 2.61799
    c: Coincident(g5,g0)
    c: Coincident(g5,g4)
    c: Tangent(g1,g2) = -1.5708
    c: Coincident(g6,g1)
    c: Tangent(g6,g2)
    c: Coincident(g6,g0)
    c: Diameter(g0) = 120
    c: PointOnObject(g7,g4)
    c: PointOnObject(g7,g2)
    c: DistanceY(g4) = 208.875
    c: Distance(g4,g0) = 16.7432  'major_r_offset'
    c: Coincident(g4,g-1)
    c: PointOnObject(g0,g-2)
    c: Distance(g0,g7) = 200
    c: Tangent(g3,g4) = -1.5708
FEATURE [PartDesign::Pad] Pad012
  Direction = (0,0,1)
  Length = 3
  Length2 = 10
  Profile = -> Sketch047
  ReferenceAxis = -> Sketch047 [N_Axis]
  Type = 0
FEATURE [PartDesign::CoordinateSystem] Local_CS013
  AttacherType = Attacher::AttachEngine3D
  MapMode = 5
  Support = -> [XY_Plane015]
FEATURE [PartDesign::CoordinateSystem] Local_CS016
  AttacherType = Attacher::AttachEngine3D
  AttachmentOffset = pos=(0,0,0) rot=(0,0,1;0.523599rad)
  MapMode = 5
  Placement = pos=(0,0,0) rot=(0,0,1;0.523599rad)
  Support = -> [XY_Plane015]
FEATURE [PartDesign::Plane] DatumPlane015
  Length = 81.9615
  MapMode = 5
  Placement = pos=(0,0,0) rot=(0,0,1;0.523599rad)
  ResizeMode = 0
  Support = -> [Local_CS016]
  Width = 81.9615
FEATURE [PartDesign::Plane] DatumPlane016
  Length = 79.989
  MapMode = 4
  Placement = pos=(86.82,84.1932,0) rot=(0.377964,0.654654,0.654654;2.41886rad)
  ResizeMode = 0
  Width = 61.6877
FEATURE [PartDesign::CoordinateSystem] Local_CS026
  AttacherType = Attacher::AttachEngine3D
  AttachmentOffset = pos=(0,16.7432,0) rot=(0,0,1;0.523599rad)
  MapMode = 5
  Placement = pos=(0,16.7432,0) rot=(0,0,1;0.523599rad)
  Support = -> [XY_Plane015]
FEATURE [PartDesign::SubShapeBinder] Binder041
  BindCopyOnChange = 0
  BindMode = 0
  ClaimChildren = false
  Context = -> Model [Body001003005002.Binder041.]
  Fuse = false
  MakeFace = true
  OffsetFill = false
  OffsetIntersection = false
  OffsetJoinType = 0
  OffsetOpenResult = false
  PartialLoad = false
  Relative = false
  Support = -> [Body001003005003013[Pocket041.Sketch083.]]
  _Version = 2
FEATURE [PartDesign::SubShapeBinder] Binder042
  BindCopyOnChange = 0
  BindMode = 0
  ClaimChildren = false
  Context = -> Model [Body001003005002.Binder042.]
  Fuse = false
  MakeFace = true
  OffsetFill = false
  OffsetIntersection = false
  OffsetJoinType = 0
  OffsetOpenResult = false
  PartialLoad = false
  Relative = false
  Support = -> [Body001003005003013[Pocket042.Sketch084.]]
  _Version = 2
FEATURE [PartDesign::SubShapeBinder] Binder043
  BindCopyOnChange = 0
  BindMode = 0
  ClaimChildren = false
  Context = -> Model [Body001003005002.Binder043.]
  Fuse = false
  MakeFace = true
  OffsetFill = false
  OffsetIntersection = false
  OffsetJoinType = 0
  OffsetOpenResult = false
  PartialLoad = false
  Placement = pos=(89.24,84.4317,0) rot=(0,0,1;0.523599rad)
  Relative = false
  Support = -> [Body001[Sketch043.]]
  _Version = 2
FEATURE [PartDesign::CoordinateSystem] Local_CS043
  AttacherType = Attacher::AttachEngine3D
  AttachmentOffset = pos=(119.5,28.5,0) rot=(0,0,1;0rad)
  MapMode = 5
  Placement = pos=(89.24,84.4317,0) rot=(0,0,1;0.523599rad)
  Support = -> [Local_CS016]
FEATURE [PartDesign::Pocket] Pocket086
  BaseFeature = -> Pad012
  Direction = (0,0,-1)
  Length = 5
  Length2 = 5
  Midplane = true
  Profile = -> Binder043
  Type = 1
FEATURE [PartDesign::CoordinateSystem] Local_CS044
  AttacherType = Attacher::AttachEngine3D
  AttachmentOffset = pos=(119.5,11.5,0) rot=(0,0,1;0rad)
  MapMode = 5
  Placement = pos=(97.74,69.7093,0) rot=(0,0,1;0.523599rad)
  Support = -> [Local_CS016]
FEATURE [PartDesign::SubShapeBinder] Binder046
  BindCopyOnChange = 0
  BindMode = 0
  ClaimChildren = false
  Context = -> Model [Body001003005002.Binder046.]
  Fuse = false
  MakeFace = true
  OffsetFill = false
  OffsetIntersection = false
  OffsetJoinType = 0
  OffsetOpenResult = false
  PartialLoad = false
  Placement = pos=(97.74,69.7093,0) rot=(0,0,1;0.523599rad)
  Relative = false
  Support = -> [Body001[Pocket073.Sketch073.]]
  _Version = 2
FEATURE [PartDesign::Pocket] Pocket089
  BaseFeature = -> Pocket086
  Direction = (0,0,-1)
  Length = 5
  Length2 = 5
  Midplane = true
  Profile = -> Binder046
  Type = 1
FEATURE [PartDesign::Mirrored] Mirrored014
  BaseFeature = -> Pocket089
  MirrorPlane = -> Sketch047 [V_Axis]
  Originals = -> [Pad012,Pocket086,Pocket089]
  Refine = true
FEATURE [PartDesign::Pocket] Pocket084
  BaseFeature = -> Mirrored014
  Direction = (0,0,-1)
  Length = 5
  Length2 = 5
  Midplane = true
  Profile = -> Binder041
  Type = 1
FEATURE [PartDesign::Pocket] Pocket085
  BaseFeature = -> Pocket084
  Direction = (0,0,-1)
  Length = 5
  Length2 = 5
  Midplane = true
  Profile = -> Binder042
  Type = 1
FEATURE [PartDesign::Body] Body001003005  label="basin_cover"
  Group = -> [Sketch047,Pad012,Pocket086,Pocket089,Mirrored014,Local_CS013,Local_CS016,DatumPlane015,DatumPlane016,Local_CS026,Binder041,Binder042,Pocket084,Pocket085,Binder043,Local_CS043,Local_CS044,Binder046]
  Origin = -> Origin014
  Placement = pos=(0,0,0) rot=(0,0,1;1.0472rad)
  Tip = -> Pocket085
COMPONENT P4 — recipe-attached ("basement", modeled in this document).
Construction recipe (the document's own serialized feature program — sketch geometry with constraints, then the solid features built on it; lengths are millimeters unless a unit is written):

FEATURE [Sketcher::SketchObject] Sketch048
  FullyConstrained = true
  MapMode = 5
  Support = -> [XY_Plane016]
  sketch-geometry (1):
    g0: Circle CenterX=0 CenterY=0 CenterZ=0 NormalX=0 NormalY=0 NormalZ=1 AngleXU=0 Radius=211.375
  constraints (2):
    c: Coincident(g0,g-1)
    c: Radius(g0) = 211.375
FEATURE [PartDesign::Pad] Pad013
  Direction = (0,0,1)
  Length = 3
  Length2 = 10
  Profile = -> Sketch048
  ReferenceAxis = -> Sketch048 [N_Axis]
  Type = 0
FEATURE [Sketcher::SketchObject] Sketch049
  AttachmentOffset = pos=(0,195.697,0) rot=(0,0,1;0rad)
  FullyConstrained = true
  MapMode = 5
  Placement = pos=(0,195.697,0) rot=(0,0,1;0rad)
  Support = -> [XY_Plane016]
  sketch-geometry (9):
    g0: ArcOfCircle CenterX=-11.5 CenterY=8.0875 CenterZ=0 NormalX=0 NormalY=0 NormalZ=1 AngleXU=0 Radius=1.5875 StartAngle=1.5708 EndAngle=4.71239
    g1: LineSegment StartX=-11.5 StartY=6.5 StartZ=0 EndX=8.325 EndY=6.5 EndZ=0
    g2: LineSegment StartX=8.325 StartY=6.5 StartZ=0 EndX=8.325 EndY=0 EndZ=0
    g3: LineSegment StartX=8.325 StartY=0 StartZ=0 EndX=11.5 EndY=0 EndZ=0
    g4: LineSegment StartX=11.5 StartY=0 StartZ=0 EndX=11.5 EndY=6.5 EndZ=0
    g5: LineSegment StartX=-11.5 StartY=9.675 StartZ=0 EndX=8.325 EndY=9.675 EndZ=0
    g6: ArcOfCircle CenterX=8.325 CenterY=6.5 CenterZ=0 NormalX=0 NormalY=0 NormalZ=1 AngleXU=0 Radius=3.175 StartAngle=6e-16 EndAngle=1.5708
    g7: GeomPoint X=8.325 Y=-6.5 Z=0
    g8: GeomPoint X=8.325 Y=-9.675 Z=0
  constraints (21):
    c: Horizontal(g1)
    c: PointOnObject(g2,g-1)
    c: Vertical(g2)
    c: Coincident(g3,g2)
    c: PointOnObject(g3,g-1)
    c: Coincident(g4,g3)
    c: Vertical(g4)
    c: Horizontal(g5)
    c: Tangent(g6,g4) = -1.5708
    c: Tangent(g6,g5) = 1.5708
    c: DistanceX(g3) = 11.5
    c: Tangent(g1,g0) = -1.5708
    c: Tangent(g5,g0) = 1.5708
    c: Diameter(g0) = 3.175
    c: DistanceX(g0) = -11.5
    c: Coincident(g6,g2)
    c: Coincident(g2,g1)
    c: Symmetric(g7,g1,g2)
    c: DistanceY(g7,g1) = 13  'cut_width'
    c: Symmetric(g8,g5,g2)
    c: DistanceY(g8,g5) = 19.35  'total_width'
FEATURE [Sketcher::SketchObject] Sketch050
  AttachmentOffset = pos=(0,195.697,0) rot=(0,0,1;0rad)
  FullyConstrained = true
  MapMode = 5
  Placement = pos=(0,195.697,0) rot=(0,0,1;0rad)
  Support = -> [XY_Plane016]
  sketch-geometry (17):
    g0: LineSegment StartX=-11.5 StartY=-8.0875 StartZ=0 EndX=-11.5 EndY=8.0875 EndZ=0
    g1: ArcOfCircle CenterX=-11.5 CenterY=8.0875 CenterZ=0 NormalX=0 NormalY=0 NormalZ=1 AngleXU=0 Radius=1.5875 StartAngle=1.5708 EndAngle=4.71239
    g2: LineSegment StartX=-11.5 StartY=6.5 StartZ=0 EndX=8.325 EndY=6.5 EndZ=0
    g3: LineSegment StartX=8.325 StartY=6.5 StartZ=0 EndX=8.325 EndY=0 EndZ=0
    g4: LineSegment StartX=8.325 StartY=0 StartZ=0 EndX=11.5 EndY=0 EndZ=0
    g5: LineSegment StartX=11.5 StartY=0 StartZ=0 EndX=11.5 EndY=6.5 EndZ=0
    g6: LineSegment StartX=-11.5 StartY=9.675 StartZ=0 EndX=8.325 EndY=9.675 EndZ=0
    g7: ArcOfCircle CenterX=8.325 CenterY=6.5 CenterZ=0 NormalX=0 NormalY=0 NormalZ=1 AngleXU=0 Radius=3.175 StartAngle=1.83e-14 EndAngle=1.5708
    g8: GeomPoint X=8.325 Y=-6.5 Z=0
    g9: ArcOfCircle CenterX=-11.5 CenterY=11.5875 CenterZ=0 NormalX=0 NormalY=0 NormalZ=1 AngleXU=0 Radius=1.5875 StartAngle=1.5708 EndAngle=4.71239
    g10: LineSegment StartX=-11.5 StartY=10 StartZ=0 EndX=8.325 EndY=10 EndZ=0
    g11: LineSegment StartX=8.325 StartY=10 StartZ=0 EndX=8.325 EndY=0 EndZ=0
    g12: LineSegment StartX=8.325 StartY=0 StartZ=0 EndX=11.5 EndY=0 EndZ=0
    g13: LineSegment StartX=11.5 StartY=0 StartZ=0 EndX=11.5 EndY=10 EndZ=0
    g14: LineSegment StartX=-11.5 StartY=13.175 StartZ=0 EndX=8.325 EndY=13.175 EndZ=0
    g15: ArcOfCircle CenterX=8.325 CenterY=10 CenterZ=0 NormalX=0 NormalY=0 NormalZ=1 AngleXU=0 Radius=3.175 StartAngle=1.5915e-12 EndAngle=1.5708
    g16: GeomPoint X=8.325 Y=-10 Z=0
  constraints (40):
    c: Horizontal(g2)
    c: PointOnObject(g3,g-1)
    c: Vertical(g3)
    c: Coincident(g4,g3)
    c: PointOnObject(g4,g-1)
    c: Coincident(g5,g4)
    c: Vertical(g5)
    c: Horizontal(g6)
    c: Tangent(g7,g5) = -1.5708
    c: Tangent(g7,g6) = 1.5708
    c: DistanceX(g4) = 11.5
    c: Tangent(g2,g1) = -1.5708
    c: Tangent(g6,g1) = 1.5708
    c: Diameter(g1) = 3.175
    c: DistanceX(g1) = -11.5
    c: Coincident(g7,g3)
    c: Coincident(g3,g2)
    c: Symmetric(g8,g2,g3)
    c: DistanceY(g8,g2) = 13  'cut_width'
    c: Horizontal(g10)
    c: PointOnObject(g11,g-1)
    c: Vertical(g11)
    c: Coincident(g12,g11)
    c: PointOnObject(g12,g-1)
    c: Coincident(g13,g12)
    c: Vertical(g13)
    c: Horizontal(g14)
    c: Tangent(g15,g13) = -1.5708
    c: Tangent(g15,g14) = 1.5708
    c: DistanceX(g12) = 11.5
    c: Tangent(g10,g9) = -1.5708
    c: Tangent(g14,g9) = 1.5708
    c: Diameter(g9) = 3.175
    c: DistanceX(g9) = -11.5
    c: Coincident(g15,g11)
    c: Coincident(g11,g10)
    c: Symmetric(g16,g10,g11)
    c: DistanceY(g16,g10) = 20  'cut_width'
    c: Coincident(g0,g1)
    c: Symmetric(g0,g0,g-1)
FEATURE [PartDesign::CoordinateSystem] Local_CS017
  AttacherType = Attacher::AttachEngine3D
  AttachmentOffset = pos=(0,0,3) rot=(0,0,1;0rad)
  MapMode = 5
  Placement = pos=(0,0,3) rot=(0,0,1;0rad)
  Support = -> [XY_Plane016]
FEATURE [PartDesign::SubShapeBinder] Binder004
  AttacherType = Attacher::AttachEngine3D
  AttachmentOffset = pos=(0,195.697,0) rot=(0,0,1;3.14159rad)
  BindCopyOnChange = 0
  BindMode = 0
  ClaimChildren = false
  Context = -> Model [Body001003005003002.Binder004.]
  Fuse = false
  MakeFace = true
  MapMode = 5
  OffsetFill = false
  OffsetIntersection = false
  OffsetJoinType = 0
  OffsetOpenResult = false
  PartialLoad = false
  Placement = pos=(0,179.522,0) rot=(0,0,1;3.14159rad)
  Relative = false
  _Version = 2
FEATURE [PartDesign::Plane] DatumPlane017
  Length = 60
  MapMode = 3
  Placement = pos=(0,179.522,0) rot=(0,0.707107,0.707107;3.14159rad)
  ResizeMode = 0
  Support = -> [Binder004]
  Width = 60
FEATURE [Sketcher::SketchObject] Sketch051
  AttachmentOffset = pos=(0,179.522,0) rot=(0,0,1;0rad)
  FullyConstrained = true
  MapMode = 5
  Placement = pos=(0,179.522,0) rot=(0,0,1;0rad)
  Support = -> [XY_Plane016]
  sketch-geometry (9):
    g0: ArcOfCircle CenterX=-11.5 CenterY=8.0875 CenterZ=0 NormalX=0 NormalY=0 NormalZ=1 AngleXU=0 Radius=1.5875 StartAngle=1.5708 EndAngle=4.71239
    g1: LineSegment StartX=-11.5 StartY=6.5 StartZ=0 EndX=8.325 EndY=6.5 EndZ=0
    g2: LineSegment StartX=8.325 StartY=6.5 StartZ=0 EndX=8.325 EndY=0 EndZ=0
    g3: LineSegment StartX=8.325 StartY=0 StartZ=0 EndX=11.5 EndY=0 EndZ=0
    g4: LineSegment StartX=11.5 StartY=0 StartZ=0 EndX=11.5 EndY=6.5 EndZ=0
    g5: LineSegment StartX=-11.5 StartY=9.675 StartZ=0 EndX=8.325 EndY=9.675 EndZ=0
    g6: ArcOfCircle CenterX=8.325 CenterY=6.5 CenterZ=0 NormalX=0 NormalY=0 NormalZ=1 AngleXU=0 Radius=3.175 StartAngle=0 EndAngle=1.5708
    g7: GeomPoint X=8.325 Y=-6.5 Z=0
    g8: LineSegment StartX=11.5 StartY=8.0875 StartZ=0 EndX=11.5 EndY=-8.0875 EndZ=0
  constraints (22):
    c: Horizontal(g1)
    c: PointOnObject(g2,g-1)
    c: Vertical(g2)
    c: Coincident(g3,g2)
    c: PointOnObject(g3,g-1)
    c: Coincident(g4,g3)
    c: Vertical(g4)
    c: Horizontal(g5)
    c: Tangent(g6,g4) = -1.5708
    c: Tangent(g6,g5) = 1.5708
    c: DistanceX(g3) = 11.5
    c: Tangent(g1,g0) = -1.5708
    c: Tangent(g5,g0) = 1.5708
    c: Diameter(g0) = 3.175
    c: DistanceX(g0) = -11.5
    c: Coincident(g6,g2)
    c: Coincident(g2,g1)
    c: Symmetric(g7,g1,g2)
    c: DistanceY(g7,g1) = 13  'cut_width'
    c: Vertical(g8)
    c: Symmetric(g0,g8,g-1)
    c: Horizontal(g8,g0)
FEATURE [PartDesign::SubShapeBinder] Binder005
  AttacherType = Attacher::AttachEngine3D
  AttachmentOffset = pos=(0,0,0) rot=(0,0,1;1.0472rad)
  BindCopyOnChange = 0
  BindMode = 0
  ClaimChildren = false
  Context = -> Body001003005003 [Binder005.]
  Fuse = false
  MakeFace = true
  MapMode = 5
  OffsetFill = false
  OffsetIntersection = false
  OffsetJoinType = 0
  OffsetOpenResult = false
  PartialLoad = false
  Placement = pos=(0,0,0) rot=(0,0,1;1.0472rad)
  Relative = false
  _Version = 2
FEATURE [PartDesign::Plane] DatumPlane018
  Length = 79.989
  MapMode = 4
  Placement = pos=(0,0,0) rot=(0.186157,0.694747,0.694747;2.77349rad)
  ResizeMode = 0
  Support = -> [Binder005]
  Width = 61.6877
FEATURE [Sketcher::SketchObject] Sketch057
  AttachmentOffset = pos=(195.697,-11.5,0) rot=(0,0,1;0rad)
  FullyConstrained = true
  MapMode = 5
  Placement = pos=(4.6e-14,195.697,-11.5) rot=(0.57735,0.57735,0.57735;2.0944rad)
  Support = -> [YZ_Plane015]
  sketch-geometry (1):
    g0: Circle CenterX=0 CenterY=0 CenterZ=0 NormalX=0 NormalY=0 NormalZ=1 AngleXU=0 Radius=1.7
  constraints (2):
    c: Coincident(g0,g-1)
    c: Diameter(g0) = 3.4
FEATURE [Sketcher::SketchObject] Sketch058
  AttachmentOffset = pos=(179.522,-11.5,0) rot=(0,0,1;0rad)
  FullyConstrained = true
  MapMode = 5
  Placement = pos=(4.24e-14,179.522,-11.5) rot=(0.57735,0.57735,0.57735;2.0944rad)
  Support = -> [YZ_Plane015]
  sketch-geometry (1):
    g0: Circle CenterX=0 CenterY=0 CenterZ=0 NormalX=0 NormalY=0 NormalZ=1 AngleXU=0 Radius=1.7
  constraints (2):
    c: Coincident(g0,g-1)
    c: Diameter(g0) = 3.4
FEATURE [PartDesign::Pocket] Pocket027
  BaseFeature = -> Pad013
  Direction = (-1,2e-16,-3e-16)
  Length = 5
  Length2 = 5
  Midplane = true
  Profile = -> Sketch058
  ReferenceAxis = -> Sketch058 [N_Axis]
  Type = 1
FEATURE [PartDesign::CoordinateSystem] Local_CS021
  AttacherType = Attacher::AttachEngine3D
  AttachmentOffset = pos=(0,0,0) rot=(0,0,1;2.0944rad)
  MapMode = 5
  Placement = pos=(0,0,0) rot=(0,0,1;2.0944rad)
  Support = -> [XY_Plane016]
FEATURE [PartDesign::CoordinateSystem] Local_CS022
  AttacherType = Attacher::AttachEngine3D
  AttachmentOffset = pos=(0,0,0) rot=(0,0,-1;2.0944rad)
  MapMode = 5
  Placement = pos=(0,0,0) rot=(0,0,-1;2.0944rad)
  Support = -> [XY_Plane016]
FEATURE [PartDesign::Plane] DatumPlane019
  Length = 81.9615
  MapMode = 5
  Placement = pos=(0,0,0) rot=(0,0,1;2.0944rad)
  ResizeMode = 0
  Support = -> [Local_CS021]
  Width = 81.9615
FEATURE [PartDesign::Plane] DatumPlane020
  Length = 81.9615
  MapMode = 5
  Placement = pos=(0,0,0) rot=(0,0,-1;2.0944rad)
  ResizeMode = 0
  Support = -> [Local_CS022]
  Width = 81.9615
FEATURE [Sketcher::SketchObject] Sketch061
  AttachmentOffset = pos=(0,195.697,0) rot=(0,0,1;0rad)
  FullyConstrained = true
  MapMode = 5
  Placement = pos=(-169.478,-97.8483,0) rot=(0,0,1;2.0944rad)
  Support = -> [DatumPlane019]
  sketch-geometry (17):
    g0: LineSegment StartX=-11.5 StartY=-8.0875 StartZ=0 EndX=-11.5 EndY=8.0875 EndZ=0
    g1: ArcOfCircle CenterX=-11.5 CenterY=8.0875 CenterZ=0 NormalX=0 NormalY=0 NormalZ=1 AngleXU=0 Radius=1.5875 StartAngle=1.5708 EndAngle=4.71239
    g2: LineSegment StartX=-11.5 StartY=6.5 StartZ=0 EndX=8.325 EndY=6.5 EndZ=0
    g3: LineSegment StartX=8.325 StartY=6.5 StartZ=0 EndX=8.325 EndY=0 EndZ=0
    g4: LineSegment StartX=8.325 StartY=0 StartZ=0 EndX=11.5 EndY=0 EndZ=0
    g5: LineSegment StartX=11.5 StartY=0 StartZ=0 EndX=11.5 EndY=6.5 EndZ=0
    g6: LineSegment StartX=-11.5 StartY=9.675 StartZ=0 EndX=8.325 EndY=9.675 EndZ=0
    g7: ArcOfCircle CenterX=8.325 CenterY=6.5 CenterZ=0 NormalX=0 NormalY=0 NormalZ=1 AngleXU=0 Radius=3.175 StartAngle=0 EndAngle=1.5708
    g8: GeomPoint X=8.325 Y=-6.5 Z=0
    g9: ArcOfCircle CenterX=-11.5 CenterY=11.5875 CenterZ=0 NormalX=0 NormalY=0 NormalZ=1 AngleXU=0 Radius=1.5875 StartAngle=1.5708 EndAngle=4.71239
    g10: LineSegment StartX=-11.5 StartY=10 StartZ=0 EndX=8.325 EndY=10 EndZ=0
    g11: LineSegment StartX=8.325 StartY=10 StartZ=0 EndX=8.325 EndY=0 EndZ=0
    g12: LineSegment StartX=8.325 StartY=0 StartZ=0 EndX=11.5 EndY=0 EndZ=0
    g13: LineSegment StartX=11.5 StartY=0 StartZ=0 EndX=11.5 EndY=10 EndZ=0
    g14: LineSegment StartX=-11.5 StartY=13.175 StartZ=0 EndX=8.325 EndY=13.175 EndZ=0
    g15: ArcOfCircle CenterX=8.325 CenterY=10 CenterZ=0 NormalX=0 NormalY=0 NormalZ=1 AngleXU=0 Radius=3.175 StartAngle=1.5915e-12 EndAngle=1.5708
    g16: GeomPoint X=8.325 Y=-10 Z=0
  constraints (40):
    c: Horizontal(g2)
    c: PointOnObject(g3,g-1)
    c: Vertical(g3)
    c: Coincident(g4,g3)
    c: PointOnObject(g4,g-1)
    c: Coincident(g5,g4)
    c: Vertical(g5)
    c: Horizontal(g6)
    c: Tangent(g7,g5) = -1.5708
    c: Tangent(g7,g6) = 1.5708
    c: DistanceX(g4) = 11.5
    c: Tangent(g2,g1) = -1.5708
    c: Tangent(g6,g1) = 1.5708
    c: Diameter(g1) = 3.175
    c: DistanceX(g1) = -11.5
    c: Coincident(g7,g3)
    c: Coincident(g3,g2)
    c: Symmetric(g8,g2,g3)
    c: DistanceY(g8,g2) = 13  'cut_width'
    c: Horizontal(g10)
    c: PointOnObject(g11,g-1)
    c: Vertical(g11)
    c: Coincident(g12,g11)
    c: PointOnObject(g12,g-1)
    c: Coincident(g13,g12)
    c: Vertical(g13)
    c: Horizontal(g14)
    c: Tangent(g15,g13) = -1.5708
    c: Tangent(g15,g14) = 1.5708
    c: DistanceX(g12) = 11.5
    c: Tangent(g10,g9) = -1.5708
    c: Tangent(g14,g9) = 1.5708
    c: Diameter(g9) = 3.175
    c: DistanceX(g9) = -11.5
    c: Coincident(g15,g11)
    c: Coincident(g11,g10)
    c: Symmetric(g16,g10,g11)
    c: DistanceY(g16,g10) = 20  'cut_width'
    c: Coincident(g0,g1)
    c: Symmetric(g0,g0,g-1)
FEATURE [Sketcher::SketchObject] Sketch062
  AttachmentOffset = pos=(0,195.697,0) rot=(0,0,1;0rad)
  FullyConstrained = true
  MapMode = 5
  Placement = pos=(169.478,-97.8483,0) rot=(0,0,-1;2.0944rad)
  Support = -> [DatumPlane020]
  sketch-geometry (17):
    g0: LineSegment StartX=-11.5 StartY=-8.0875 StartZ=0 EndX=-11.5 EndY=8.0875 EndZ=0
    g1: ArcOfCircle CenterX=-11.5 CenterY=8.0875 CenterZ=0 NormalX=0 NormalY=0 NormalZ=1 AngleXU=0 Radius=1.5875 StartAngle=1.5708 EndAngle=4.71239
    g2: LineSegment StartX=-11.5 StartY=6.5 StartZ=0 EndX=8.325 EndY=6.5 EndZ=0
    g3: LineSegment StartX=8.325 StartY=6.5 StartZ=0 EndX=8.325 EndY=0 EndZ=0
    g4: LineSegment StartX=8.325 StartY=0 StartZ=0 EndX=11.5 EndY=0 EndZ=0
    g5: LineSegment StartX=11.5 StartY=0 StartZ=0 EndX=11.5 EndY=6.5 EndZ=0
    g6: LineSegment StartX=-11.5 StartY=9.675 StartZ=0 EndX=8.325 EndY=9.675 EndZ=0
    g7: ArcOfCircle CenterX=8.325 CenterY=6.5 CenterZ=0 NormalX=0 NormalY=0 NormalZ=1 AngleXU=0 Radius=3.175 StartAngle=0 EndAngle=1.5708
    g8: GeomPoint X=8.325 Y=-6.5 Z=0
    g9: ArcOfCircle CenterX=-11.5 CenterY=11.5875 CenterZ=0 NormalX=0 NormalY=0 NormalZ=1 AngleXU=0 Radius=1.5875 StartAngle=1.5708 EndAngle=4.71239
    g10: LineSegment StartX=-11.5 StartY=10 StartZ=0 EndX=8.325 EndY=10 EndZ=0
    g11: LineSegment StartX=8.325 StartY=10 StartZ=0 EndX=8.325 EndY=0 EndZ=0
    g12: LineSegment StartX=8.325 StartY=0 StartZ=0 EndX=11.5 EndY=0 EndZ=0
    g13: LineSegment StartX=11.5 StartY=0 StartZ=0 EndX=11.5 EndY=10 EndZ=0
    g14: LineSegment StartX=-11.5 StartY=13.175 StartZ=0 EndX=8.325 EndY=13.175 EndZ=0
    g15: ArcOfCircle CenterX=8.325 CenterY=10 CenterZ=0 NormalX=0 NormalY=0 NormalZ=1 AngleXU=0 Radius=3.175 StartAngle=1.5915e-12 EndAngle=1.5708
    g16: GeomPoint X=8.325 Y=-10 Z=0
  constraints (40):
    c: Horizontal(g2)
    c: PointOnObject(g3,g-1)
    c: Vertical(g3)
    c: Coincident(g4,g3)
    c: PointOnObject(g4,g-1)
    c: Coincident(g5,g4)
    c: Vertical(g5)
    c: Horizontal(g6)
    c: Tangent(g7,g5) = -1.5708
    c: Tangent(g7,g6) = 1.5708
    c: DistanceX(g4) = 11.5
    c: Tangent(g2,g1) = -1.5708
    c: Tangent(g6,g1) = 1.5708
    c: Diameter(g1) = 3.175
    c: DistanceX(g1) = -11.5
    c: Coincident(g7,g3)
    c: Coincident(g3,g2)
    c: Symmetric(g8,g2,g3)
    c: DistanceY(g8,g2) = 13  'cut_width'
    c: Horizontal(g10)
    c: PointOnObject(g11,g-1)
    c: Vertical(g11)
    c: Coincident(g12,g11)
    c: PointOnObject(g12,g-1)
    c: Coincident(g13,g12)
    c: Vertical(g13)
    c: Horizontal(g14)
    c: Tangent(g15,g13) = -1.5708
    c: Tangent(g15,g14) = 1.5708
    c: DistanceX(g12) = 11.5
    c: Tangent(g10,g9) = -1.5708
    c: Tangent(g14,g9) = 1.5708
    c: Diameter(g9) = 3.175
    c: DistanceX(g9) = -11.5
    c: Coincident(g15,g11)
    c: Coincident(g11,g10)
    c: Symmetric(g16,g10,g11)
    c: DistanceY(g16,g10) = 20  'cut_width'
    c: Coincident(g0,g1)
    c: Symmetric(g0,g0,g-1)
FEATURE [Sketcher::SketchObject] Sketch063
  AttachmentOffset = pos=(0,179.522,0) rot=(0,0,1;0rad)
  FullyConstrained = true
  MapMode = 5
  Placement = pos=(-155.47,-89.7608,0) rot=(0,0,1;2.0944rad)
  Support = -> [DatumPlane019]
  sketch-geometry (9):
    g0: ArcOfCircle CenterX=-11.5 CenterY=8.0875 CenterZ=0 NormalX=0 NormalY=0 NormalZ=1 AngleXU=0 Radius=1.5875 StartAngle=1.5708 EndAngle=4.71239
    g1: LineSegment StartX=-11.5 StartY=6.5 StartZ=0 EndX=8.325 EndY=6.5 EndZ=0
    g2: LineSegment StartX=8.325 StartY=6.5 StartZ=0 EndX=8.325 EndY=0 EndZ=0
    g3: LineSegment StartX=8.325 StartY=0 StartZ=0 EndX=11.5 EndY=0 EndZ=0
    g4: LineSegment StartX=11.5 StartY=0 StartZ=0 EndX=11.5 EndY=6.5 EndZ=0
    g5: LineSegment StartX=-11.5 StartY=9.675 StartZ=0 EndX=8.325 EndY=9.675 EndZ=0
    g6: ArcOfCircle CenterX=8.325 CenterY=6.5 CenterZ=0 NormalX=0 NormalY=0 NormalZ=1 AngleXU=0 Radius=3.175 StartAngle=0 EndAngle=1.5708
    g7: GeomPoint X=8.325 Y=-6.5 Z=0
    g8: LineSegment StartX=11.5 StartY=8.0875 StartZ=0 EndX=11.5 EndY=-8.0875 EndZ=0
  constraints (22):
    c: Horizontal(g1)
    c: PointOnObject(g2,g-1)
    c: Vertical(g2)
    c: Coincident(g3,g2)
    c: PointOnObject(g3,g-1)
    c: Coincident(g4,g3)
    c: Vertical(g4)
    c: Horizontal(g5)
    c: Tangent(g6,g4) = -1.5708
    c: Tangent(g6,g5) = 1.5708
    c: DistanceX(g3) = 11.5
    c: Tangent(g1,g0) = -1.5708
    c: Tangent(g5,g0) = 1.5708
    c: Diameter(g0) = 3.175
    c: DistanceX(g0) = -11.5
    c: Coincident(g6,g2)
    c: Coincident(g2,g1)
    c: Symmetric(g7,g1,g2)
    c: DistanceY(g7,g1) = 13  'cut_width'
    c: Vertical(g8)
    c: Symmetric(g0,g8,g-1)
    c: Horizontal(g8,g0)
FEATURE [Sketcher::SketchObject] Sketch064
  AttachmentOffset = pos=(0,179.522,0) rot=(0,0,1;0rad)
  FullyConstrained = true
  MapMode = 5
  Placement = pos=(155.47,-89.7608,0) rot=(0,0,-1;2.0944rad)
  Support = -> [DatumPlane020]
  sketch-geometry (9):
    g0: ArcOfCircle CenterX=-11.5 CenterY=8.0875 CenterZ=0 NormalX=0 NormalY=0 NormalZ=1 AngleXU=0 Radius=1.5875 StartAngle=1.5708 EndAngle=4.71239
    g1: LineSegment StartX=-11.5 StartY=6.5 StartZ=0 EndX=8.325 EndY=6.5 EndZ=0
    g2: LineSegment StartX=8.325 StartY=6.5 StartZ=0 EndX=8.325 EndY=0 EndZ=0
    g3: LineSegment StartX=8.325 StartY=0 StartZ=0 EndX=11.5 EndY=0 EndZ=0
    g4: LineSegment StartX=11.5 StartY=0 StartZ=0 EndX=11.5 EndY=6.5 EndZ=0
    g5: LineSegment StartX=-11.5 StartY=9.675 StartZ=0 EndX=8.325 EndY=9.675 EndZ=0
    g6: ArcOfCircle CenterX=8.325 CenterY=6.5 CenterZ=0 NormalX=0 NormalY=0 NormalZ=1 AngleXU=0 Radius=3.175 StartAngle=0 EndAngle=1.5708
    g7: GeomPoint X=8.325 Y=-6.5 Z=0
    g8: LineSegment StartX=11.5 StartY=8.0875 StartZ=0 EndX=11.5 EndY=-8.0875 EndZ=0
  constraints (22):
    c: Horizontal(g1)
    c: PointOnObject(g2,g-1)
    c: Vertical(g2)
    c: Coincident(g3,g2)
    c: PointOnObject(g3,g-1)
    c: Coincident(g4,g3)
    c: Vertical(g4)
    c: Horizontal(g5)
    c: Tangent(g6,g4) = -1.5708
    c: Tangent(g6,g5) = 1.5708
    c: DistanceX(g3) = 11.5
    c: Tangent(g1,g0) = -1.5708
    c: Tangent(g5,g0) = 1.5708
    c: Diameter(g0) = 3.175
    c: DistanceX(g0) = -11.5
    c: Coincident(g6,g2)
    c: Coincident(g2,g1)
    c: Symmetric(g7,g1,g2)
    c: DistanceY(g7,g1) = 13  'cut_width'
    c: Vertical(g8)
    c: Symmetric(g0,g8,g-1)
    c: Horizontal(g8,g0)
FEATURE [Sketcher::SketchObject] Sketch075
  AttachmentOffset = pos=(0,0,0) rot=(0,0,1;3.14159rad)
  FullyConstrained = true
  MapMode = 5
  Placement = pos=(0,0,0) rot=(0,0,1;3.14159rad)
  Support = -> [XY_Plane016]
  sketch-geometry (6):
    g0: Circle CenterX=64.8152 CenterY=64.8152 CenterZ=0 NormalX=0 NormalY=0 NormalZ=1 AngleXU=0 Radius=1.7
    g1: Circle CenterX=64.8152 CenterY=-64.8152 CenterZ=0 NormalX=0 NormalY=0 NormalZ=1 AngleXU=0 Radius=1.7
    g2: Circle CenterX=-64.8152 CenterY=-64.8152 CenterZ=0 NormalX=0 NormalY=0 NormalZ=1 AngleXU=0 Radius=1.7
    g3: Circle CenterX=-64.8152 CenterY=64.8152 CenterZ=0 NormalX=0 NormalY=0 NormalZ=1 AngleXU=0 Radius=1.7
    g4: LineSegment StartX=-64.8152 StartY=64.8152 StartZ=0 EndX=64.8152 EndY=64.8152 EndZ=0
    g5: LineSegment StartX=64.8152 StartY=64.8152 StartZ=0 EndX=64.8152 EndY=-64.8152 EndZ=0
  constraints (13):
    c: Symmetric(g3,g0,g-2)
    c: Symmetric(g0,g1,g-1)
    c: Symmetric(g0,g2,g-1)
    c: Equal(g0,g3)
    c: Equal(g0,g2)
    c: Equal(g0,g1)
    c: Diameter(g0) = 3.4
    c: Coincident(g4,g3)
    c: Coincident(g4,g0)
    c: Coincident(g5,g0)
    c: Coincident(g5,g1)
    c: Equal(g5,g4)
    c: Distance(g2,g0) = 183.325
FEATURE [PartDesign::Pocket] Pocket036
  BaseFeature = -> Pocket027
  Direction = (0,0,-1)
  Length = 5
  Length2 = 5
  Midplane = true
  Profile = -> Sketch075
  ReferenceAxis = -> Sketch075 [N_Axis]
  Type = 1
FEATURE [PartDesign::SubShapeBinder] Binder018
  BindCopyOnChange = 0
  BindMode = 0
  ClaimChildren = true
  Context = -> Body001003005003 [Binder018.]
  Fuse = false
  MakeFace = true
  OffsetFill = false
  OffsetIntersection = false
  OffsetJoinType = 0
  OffsetOpenResult = false
  PartialLoad = false
  Relative = false
  Support = -> [Body001003005003012[Pocket039.Sketch080.]]
  _Version = 2
FEATURE [PartDesign::SubShapeBinder] Binder023
  BindCopyOnChange = 0
  BindMode = 0
  ClaimChildren = false
  Context = -> Body001003005003 [Binder023.]
  Fuse = false
  MakeFace = true
  OffsetFill = false
  OffsetIntersection = false
  OffsetJoinType = 0
  OffsetOpenResult = false
  PartialLoad = false
  Relative = true
  Support = -> [Body001003005003013[Pocket042.Sketch084.,Pocket041.Sketch083.]]
  _Version = 2
FEATURE [PartDesign::SubShapeBinder] Binder036
  BindCopyOnChange = 0
  BindMode = 0
  ClaimChildren = false
  Context = -> Body001003005003 [Binder036.]
  Fuse = false
  MakeFace = true
  OffsetFill = false
  OffsetIntersection = false
  OffsetJoinType = 0
  OffsetOpenResult = false
  PartialLoad = false
  Placement = pos=(11.5,180,0) rot=(0,0,1;1.5708rad)
  Relative = true
  Support = -> [Body_7[Pocket061.Sketch105.]]
  _Version = 2
FEATURE [PartDesign::Pocket] Pocket074
  BaseFeature = -> Pocket036
  Direction = (0,0,-1)
  Length = 5
  Length2 = 5
  Midplane = true
  Profile = -> Binder036
  Type = 1
FEATURE [PartDesign::Mirrored] Mirrored
  MirrorPlane = -> YZ_Plane015
FEATURE [PartDesign::PolarPattern] PolarPattern015
  Angle = 360
  Axis = -> Z_Axis015
  Occurrences = 3
FEATURE [PartDesign::MultiTransform] MultiTransform
  BaseFeature = -> Pocket074
  Originals = -> [Pocket074]
  Transformations = -> [Mirrored,PolarPattern015]
FEATURE [Sketcher::SketchObject] Sketch120
  AttachmentOffset = pos=(0,-70,0) rot=(0,0,1;0rad)
  FullyConstrained = true
  MapMode = 5
  Placement = pos=(0,-70,0) rot=(0,0,1;0rad)
  Support = -> [XY_Plane016]
  sketch-geometry (1):
    g0: Circle CenterX=0 CenterY=0 CenterZ=0 NormalX=0 NormalY=0 NormalZ=1 AngleXU=0 Radius=4.25
  constraints (2):
    c: Coincident(g0,g-1)
    c: Diameter(g0) = 8.5
FEATURE [PartDesign::Pocket] Pocket087
  BaseFeature = -> MultiTransform
  Direction = (0,0,-1)
  Length = 5
  Length2 = 5
  Midplane = true
  Profile = -> Binder023
  Type = 1
FEATURE [PartDesign::PolarPattern] PolarPattern018
  Angle = 120
  Axis = -> Z_Axis015
  BaseFeature = -> Pocket087
  Occurrences = 2
  Originals = -> [Pocket087]
FEATURE [Sketcher::SketchObject] Sketch132
  FullyConstrained = true
  MapMode = 5
  Support = -> [XY_Plane016]
  sketch-geometry (3):
    g0: Circle CenterX=0 CenterY=0 CenterZ=0 NormalX=0 NormalY=0 NormalZ=1 AngleXU=0 Radius=211.375
    g1: Circle CenterX=0 CenterY=0 CenterZ=0 NormalX=0 NormalY=0 NormalZ=1 AngleXU=0 Radius=201.375
    g2: LineSegment StartX=201.375 StartY=0 StartZ=0 EndX=211.375 EndY=0 EndZ=0
  constraints (8):
    c: Coincident(g0,g-1)
    c: Radius(g0) = 211.375
    c: Coincident(g1,g0)
    c: PointOnObject(g2,g1)
    c: PointOnObject(g2,g0)
    c: Horizontal(g2)
    c: PointOnObject(g0,g2)
    c: DistanceX(g2,g2) = 10
FEATURE [PartDesign::Pad] Pad030
  BaseFeature = -> PolarPattern018
  Direction = (0,0,1)
  Length = 3
  Length2 = 10
  Profile = -> Sketch132
  ReferenceAxis = -> Sketch132 [N_Axis]
  Type = 0
FEATURE [PartDesign::Body] Body001003005003  label="basement"
  Group = -> [Sketch048,Pad013,Sketch049,Binder004,DatumPlane017,Sketch050,Local_CS017,Sketch051,Binder005,DatumPlane018,Sketch057,Sketch058,Pocket027,Local_CS021,Local_CS022,DatumPlane019,DatumPlane020,Sketch061,Sketch062,Sketch063,Sketch064,Sketch075,Pocket036,Binder018,Binder023,Binder036,Pocket074,MultiTransform,Mirrored,PolarPattern015,Sketch120,Pocket087,PolarPattern018,Sketch132,Pad030]
  Origin = -> Origin015
  Tip = -> Pad030
COMPONENT P5 — recipe-attached ("Body001003005003003", modeled in this document).
Construction recipe (the document's own serialized feature program — sketch geometry with constraints, then the solid features built on it; lengths are millimeters unless a unit is written):

FEATURE [Sketcher::SketchObject] Sketch052
  FullyConstrained = true
  MapMode = 5
  Support = -> [XY_Plane017]
  sketch-geometry (6):
    g0: ArcOfCircle CenterX=0 CenterY=0 CenterZ=0 NormalX=0 NormalY=0 NormalZ=1 AngleXU=0 Radius=198.875 StartAngle=0.69333 EndAngle=1.5708
    g1: ArcOfCircle CenterX=0 CenterY=0 CenterZ=0 NormalX=0 NormalY=0 NormalZ=1 AngleXU=0 Radius=208.875 StartAngle=0.69333 EndAngle=1.5708
    g2: ArcOfCircle CenterX=156.805 CenterY=130.297 CenterZ=0 NormalX=0 NormalY=0 NormalZ=1 AngleXU=0 Radius=5 StartAngle=3.83492 EndAngle=6.97652
    g3: LineSegment StartX=1.22e-14 StartY=198.875 StartZ=0 EndX=1.28e-14 EndY=208.875 EndZ=0
    g4: ArcOfCircle CenterX=0 CenterY=0 CenterZ=0 NormalX=0 NormalY=0 NormalZ=1 AngleXU=0 Radius=203.875 StartAngle=0.668805 EndAngle=1.5708
    g5: LineSegment StartX=0 StartY=0 StartZ=0 EndX=176.561 EndY=101.938 EndZ=0
  constraints (18):
    c: Coincident(g0,g-1)
    c: PointOnObject(g0,g-2)
    c: Coincident(g1,g0)
    c: PointOnObject(g1,g-2)
    c: Coincident(g3,g1)
    c: DistanceY(g1) = 208.875  'r'
    c: DistanceY(g0,g1) = 10  'width'
    c: Tangent(g2,g0) = 1.5708
    c: Tangent(g2,g1) = -1.5708
    c: Coincident(g4,g0)
    c: PointOnObject(g4,g2)
    c: Coincident(g5,g0)
    c: Angle(g-1,g5) = 0.523599
    c: Distance(g4,g5) = 29.5
    c: Coincident(g3,g0)
    c: PointOnObject(g2,g4)
    c: PointOnObject(g4,g-2)
    c: PointOnObject(g5,g4)
FEATURE [PartDesign::Pad] Pad014
  Direction = (0,0,1)
  Length = 3
  Length2 = 10
  Profile = -> Sketch052
  ReferenceAxis = -> Sketch052 [N_Axis]
  Type = 0
FEATURE [PartDesign::CoordinateSystem] Local_CS018
  AttacherType = Attacher::AttachEngine3D
  MapMode = 5
  Support = -> [XY_Plane017]
FEATURE [Sketcher::SketchObject] Sketch055
  FullyConstrained = true
  MapMode = 5
  Support = -> [XY_Plane017]
  sketch-geometry (9):
    g0: ArcOfCircle CenterX=0 CenterY=0 CenterZ=0 NormalX=0 NormalY=0 NormalZ=1 AngleXU=0 Radius=198.875 StartAngle=0.69333 EndAngle=1.5708
    g1: ArcOfCircle CenterX=0 CenterY=0 CenterZ=0 NormalX=0 NormalY=0 NormalZ=1 AngleXU=0 Radius=208.875 StartAngle=0.69333 EndAngle=1.5708
    g2: ArcOfCircle CenterX=156.805 CenterY=130.297 CenterZ=0 NormalX=0 NormalY=0 NormalZ=1 AngleXU=0 Radius=5 StartAngle=3.83492 EndAngle=6.97652
    g3: LineSegment StartX=1.22e-14 StartY=198.875 StartZ=0 EndX=1.28e-14 EndY=208.875 EndZ=0
    g4: ArcOfCircle CenterX=0 CenterY=0 CenterZ=0 NormalX=0 NormalY=0 NormalZ=1 AngleXU=0 Radius=203.875 StartAngle=0.668805 EndAngle=1.5708
    g5: LineSegment StartX=0 StartY=0 StartZ=0 EndX=176.561 EndY=101.938 EndZ=0
    g6: LineSegment StartX=1.22e-14 StartY=202.175 StartZ=0 EndX=1.3e-14 EndY=205.575 EndZ=0
    g7: ArcOfCircle CenterX=1.25e-14 CenterY=203.875 CenterZ=0 NormalX=0 NormalY=0 NormalZ=1 AngleXU=0 Radius=1.7 StartAngle=4.71239 EndAngle=7.85398
    g8: Circle CenterX=143.11 CenterY=145.206 CenterZ=0 NormalX=0 NormalY=0 NormalZ=1 AngleXU=0 Radius=1.7
  constraints (27):
    c: Coincident(g0,g-1)
    c: PointOnObject(g0,g-2)
    c: Coincident(g1,g0)
    c: PointOnObject(g1,g-2)
    c: Coincident(g3,g1)
    c: DistanceY(g1) = 208.875  'r'
    c: DistanceY(g0,g1) = 10  'width'
    c: Tangent(g2,g0) = 1.5708
    c: Tangent(g2,g1) = -1.5708
    c: Coincident(g4,g0)
    c: PointOnObject(g4,g2)
    c: Coincident(g5,g0)
    c: Angle(g-1,g5) = 0.523599
    c: Distance(g4,g5) = 29.5
    c: Coincident(g3,g0)
    c: PointOnObject(g2,g4)
    c: PointOnObject(g4,g-2)
    c: PointOnObject(g5,g4)
    c: PointOnObject(g6,g3)
    c: PointOnObject(g6,g3)
    c: Coincident(g7,g4)
    c: Coincident(g7,g6)
    c: Coincident(g7,g6)
    c: PointOnObject(g8,g4)
    c: Equal(g8,g7)
    c: Diameter(g7) = 3.4
    c: DistanceX(g8) = 143.11
FEATURE [PartDesign::Pocket] Pocket019
  BaseFeature = -> Pad014
  Direction = (0,0,-1)
  Length = 5
  Length2 = 5
  Midplane = true
  Profile = -> Sketch055
  ReferenceAxis = -> Sketch055 [N_Axis]
  Type = 1
FEATURE [PartDesign::Mirrored] Mirrored019
  BaseFeature = -> Pocket019
  MirrorPlane = -> Sketch052 [V_Axis]
  Originals = -> [Pad014,Pocket019]
FEATURE [PartDesign::Body] Body001003005003003
  Group = -> [Sketch052,Pad014,Pocket019,Mirrored019,Local_CS018,Sketch055]
  Origin = -> Origin016
  Tip = -> Mirrored019
COMPONENT P6 — recipe-attached ("plexiglass_holder_tech_top", modeled in this document).
Construction recipe (the document's own serialized feature program — sketch geometry with constraints, then the solid features built on it; lengths are millimeters unless a unit is written):

FEATURE [PartDesign::CoordinateSystem] Local_CS019
  AttacherType = Attacher::AttachEngine3D
  MapMode = 5
  Support = -> [XY_Plane018]
FEATURE [Sketcher::SketchObject] Sketch121
  FullyConstrained = true
  MapMode = 5
  Support = -> [XY_Plane018]
  sketch-geometry (7):
    g0: ArcOfCircle CenterX=0 CenterY=0 CenterZ=0 NormalX=0 NormalY=0 NormalZ=1 AngleXU=0 Radius=196.875 StartAngle=0.763183 EndAngle=1.5708
    g1: LineSegment StartX=142.27 StartY=136.085 StartZ=0 EndX=150.91 EndY=127.052 EndZ=0
    g2: LineSegment StartX=150.91 StartY=127.052 StartZ=0 EndX=159.551 EndY=118.019 EndZ=0
    g3: LineSegment StartX=159.551 StartY=118.019 StartZ=0 EndX=141.485 EndY=100.739 EndZ=0
    g4: LineSegment StartX=0 StartY=0 StartZ=0 EndX=175.512 EndY=101.332 EndZ=0
    g5: LineSegment StartX=141.485 StartY=100.739 StartZ=0 EndX=124.204 EndY=118.805 EndZ=0
    g6: LineSegment StartX=124.204 StartY=118.805 StartZ=0 EndX=142.27 EndY=136.085 EndZ=0
  constraints (21):
    c: Coincident(g0,g-1)
    c: PointOnObject(g0,g-2)
    c: Coincident(g2,g1)
    c: Parallel(g1,g2)
    c: Equal(g2,g1)
    c: Distance(g2,g0) = 25
    c: Tangent(g1,g0) = 1.5708
    c: DistanceY(g0) = 196.875
    c: Coincident(g3,g2)
    c: Distance(g3) = 25
    c: Coincident(g4,g0)
    c: PointOnObject(g4,g2)
    c: Perpendicular(g2,g3)
    c: Angle(g-1,g4) = 0.523599
    c: Distance(g3,g4) = 16.5
    c: Distance(g2,g4) = 22.4325
    c: Coincident(g5,g3)
    c: Perpendicular(g5,g3)
    c: Coincident(g6,g5)
    c: Coincident(g6,g0)
    c: Perpendicular(g5,g6)
FEATURE [Sketcher::SketchObject] Sketch053
  ExternalGeometry = -> [Sketch121]
  FullyConstrained = true
  MapMode = 5
  Support = -> [XY_Plane018]
  sketch-geometry (7):
    g0: LineSegment StartX=1.11e-14 StartY=181.875 StartZ=0 EndX=1.21e-14 EndY=196.875 EndZ=0
    g1: ArcOfCircle CenterX=0 CenterY=0 CenterZ=0 NormalX=0 NormalY=0 NormalZ=1 AngleXU=0 Radius=181.875 StartAngle=0.768652 EndAngle=1.5708
    g2: ArcOfCircle CenterX=0 CenterY=0 CenterZ=0 NormalX=0 NormalY=0 NormalZ=1 AngleXU=0 Radius=196.875 StartAngle=0.768289 EndAngle=1.5708
    g3: LineSegment StartX=132.151 StartY=126.406 StartZ=0 EndX=141.545 EndY=135.392 EndZ=0
    g4: ArcOfCircle CenterX=140.854 CenterY=136.115 CenterZ=0 NormalX=0 NormalY=0 NormalZ=1 AngleXU=0 Radius=1 StartAngle=5.47557 EndAngle=7.05147
    g5: ArcOfCircle CenterX=131.46 CenterY=127.129 CenterZ=0 NormalX=0 NormalY=0 NormalZ=1 AngleXU=0 Radius=1 StartAngle=3.91024 EndAngle=5.47557
    g6: GeomPoint X=131.43 Y=125.717 Z=0
  constraints (18):
    c: PointOnObject(g0,g-2)
    c: PointOnObject(g0,g-2)
    c: DistanceY(g0) = 196.875
    c: Tangent(g3,g4) = -1.5708
    c: Tangent(g2,g4) = -1.5708
    c: Tangent(g3,g5) = -1.5708
    c: Tangent(g1,g5) = 1.5708
    c: Equal(g5,g4)
    c: Diameter(g5) = 2
    c: Perpendicular(g-3,g3)
    c: PointOnObject(g-3,g3)
    c: Coincident(g2,g0)
    c: Coincident(g1,g0)
    c: PointOnObject(g6,g3)
    c: PointOnObject(g6,g1)
    c: Coincident(g1,g2)
    c: DistanceY(g0,g0) = 15
    c: Coincident(g1,g-1)
FEATURE [PartDesign::Pad] Pad015
  Direction = (0,0,1)
  Length = 3
  Length2 = 10
  Profile = -> Sketch053
  ReferenceAxis = -> Sketch053 [N_Axis]
  Type = 0
FEATURE [PartDesign::Mirrored] Mirrored020
  BaseFeature = -> Pad015
  MirrorPlane = -> Sketch053 [V_Axis]
  Originals = -> [Pad015]
  Refine = true
FEATURE [Sketcher::SketchObject] Sketch054
  ExternalGeometry = -> [Sketch053]
  FullyConstrained = true
  MapMode = 5
  Support = -> [XY_Plane018]
  sketch-geometry (6):
    g0: ArcOfCircle CenterX=0 CenterY=0 CenterZ=0 NormalX=0 NormalY=0 NormalZ=1 AngleXU=0 Radius=189.373 StartAngle=0.763183 EndAngle=1.5708
    g1: Circle CenterX=129.748 CenterY=137.941 CenterZ=0 NormalX=0 NormalY=0 NormalZ=1 AngleXU=0 Radius=1.7
    g2: Circle CenterX=1.16e-14 CenterY=189.373 CenterZ=0 NormalX=0 NormalY=0 NormalZ=1 AngleXU=0 Radius=1.7
    g3: Circle CenterX=-129.748 CenterY=137.941 CenterZ=0 NormalX=0 NormalY=0 NormalZ=1 AngleXU=0 Radius=1.7
    g4: LineSegment StartX=132.151 StartY=126.406 StartZ=0 EndX=136.848 EndY=130.899 EndZ=0
    g5: LineSegment StartX=136.848 StartY=130.899 StartZ=0 EndX=141.545 EndY=135.392 EndZ=0
  constraints (15):
    c: PointOnObject(g1,g0)
    c: Diameter(g1) = 3.4
    c: Coincident(g2,g0)
    c: Equal(g2,g1)
    c: Equal(g3,g1)
    c: Symmetric(g1,g3,g-2)
    c: Coincident(g5,g4)
    c: Equal(g4,g5)
    c: Parallel(g4,g5)
    c: Coincident(g0,g4)
    c: Coincident(g0,g-1)
    c: Distance(g1,g0) = 10
    c: PointOnObject(g2,g-2)
    c: Coincident(g4,g-3)
    c: Coincident(g5,g-3)
FEATURE [PartDesign::Pocket] Pocket018
  BaseFeature = -> Mirrored020
  Direction = (0,0,-1)
  Length = 5
  Length2 = 5
  Midplane = true
  Profile = -> Sketch054
  ReferenceAxis = -> Sketch054 [N_Axis]
  Type = 1
FEATURE [PartDesign::Body] Body001003005003004  label="plexiglass_holder_tech_top"
  Group = -> [Sketch053,Pad015,Mirrored020,Pocket018,Local_CS019,Sketch054,Sketch121]
  Origin = -> Origin017
  Placement = pos=(0,0,0) rot=(0,0,1;1.0472rad)
  Tip = -> Pocket018
COMPONENT P7 — recipe-attached ("basement2", modeled in this document).
Construction recipe (the document's own serialized feature program — sketch geometry with constraints, then the solid features built on it; lengths are millimeters unless a unit is written):

FEATURE [Sketcher::SketchObject] Sketch076
  FullyConstrained = true
  MapMode = 5
  Support = -> [XY_Plane025]
  sketch-geometry (1):
    g0: Circle CenterX=0 CenterY=0 CenterZ=0 NormalX=0 NormalY=0 NormalZ=1 AngleXU=0 Radius=168.5
  constraints (2):
    c: Coincident(g0,g-1)
    c: Diameter(g0) = 337
FEATURE [PartDesign::Pad] Pad020
  Direction = (0,0,1)
  Length = 3
  Length2 = 10
  Profile = -> Sketch076
  ReferenceAxis = -> Sketch076 [N_Axis]
  Type = 0
FEATURE [PartDesign::SubShapeBinder] Binder044
  BindCopyOnChange = 0
  BindMode = 0
  ClaimChildren = false
  Context = -> Body001003005003011 [Binder044.]
  Fuse = false
  MakeFace = true
  OffsetFill = false
  OffsetIntersection = false
  OffsetJoinType = 0
  OffsetOpenResult = false
  PartialLoad = false
  Relative = true
  Support = -> [Body001003005003[Pocket036.Sketch075.]]
  _Version = 2
FEATURE [PartDesign::SubShapeBinder] Binder045
  BindCopyOnChange = 0
  BindMode = 0
  ClaimChildren = false
  Context = -> Body001003005003011 [Binder045.]
  Fuse = false
  MakeFace = true
  OffsetFill = false
  OffsetIntersection = false
  OffsetJoinType = 0
  OffsetOpenResult = false
  PartialLoad = false
  Placement = pos=(0,0,0) rot=(0,0,1;0.785398rad)
  Relative = true
  Support = -> [Body001003005003[Pocket036.Sketch075.]]
  _Version = 2
FEATURE [PartDesign::Pocket] Pocket088
  BaseFeature = -> Pad020
  Direction = (0,0,-1)
  Length = 5
  Length2 = 5
  Midplane = true
  Profile = -> Binder044
  Type = 1
FEATURE [PartDesign::Hole] Hole
  BaseFeature = -> Pocket088
  CustomThreadClearance = 0
  Depth = 25
  DepthType = 0
  Diameter = 15.5
  DrillForDepth = false
  DrillPoint = 1
  DrillPointAngle = 118
  HoleCutCountersinkAngle = 90
  HoleCutCustomValues = false
  HoleCutDepth = 0
  HoleCutDiameter = 6.1
  HoleCutType = 0
  ModelThread = false
  Profile = -> Binder045
  Reversed = true
  Tapered = false
  TaperedAngle = 90
  ThreadClass = 0
  ThreadDepth = 25
  ThreadDepthType = 0
  ThreadDirection = 0
  ThreadFit = 0
  ThreadSize = 0
  ThreadType = 0
  Threaded = false
  UseCustomThreadClearance = false
FEATURE [PartDesign::Body] Body001003005003011  label="basement2"
  Group = -> [Sketch076,Pad020,Binder044,Binder045,Pocket088,Hole]
  Origin = -> Origin024
  Tip = -> Hole
COMPONENT P8 — recipe-attached ("Body001003005003012", modeled in this document).
Construction recipe (the document's own serialized feature program — sketch geometry with constraints, then the solid features built on it; lengths are millimeters unless a unit is written):

FEATURE [Sketcher::SketchObject] Sketch078
  FullyConstrained = true
  MapMode = 5
  Placement = pos=(0,0,0) rot=(1,0,0;1.5708rad)
  Support = -> [XZ_Plane025]
FEATURE [Sketcher::SketchObject] Sketch079
  FullyConstrained = true
  MapMode = 5
  Placement = pos=(0,0,0) rot=(0.57735,0.57735,0.57735;2.0944rad)
  Support = -> [YZ_Plane025]
  sketch-geometry (3):
    g0: LineSegment StartX=15 StartY=0 StartZ=0 EndX=0 EndY=0 EndZ=0
    g1: LineSegment StartX=0 StartY=0 StartZ=0 EndX=0 EndY=157 EndZ=0
    g2: LineSegment StartX=0 StartY=157 StartZ=0 EndX=15 EndY=157 EndZ=0
  constraints (9):
    c: PointOnObject(g0,g-1)
    c: Coincident(g0,g-1)
    c: Coincident(g1,g0)
    c: PointOnObject(g1,g-2)
    c: Coincident(g2,g1)
    c: Horizontal(g2)
    c: DistanceX(g0,g0) = 15
    c: Vertical(g0,g2)
    c: DistanceY(g1) = 157
FEATURE [PartDesign::FeaturePython] BaseBend  # WARN: FeaturePython — macro-defined, semantics opaque (R4)
  BendSide = 0
  BendSketch = -> Sketch079
  MidPlane = true
  Reverse = false
  length = 15
  radius = 2
  thickness = 1
FEATURE [Sketcher::SketchObject] Sketch080
  AttachmentOffset = pos=(0,7.5,0) rot=(0,0,1;0rad)
  FullyConstrained = true
  MapMode = 5
  Placement = pos=(0,7.5,0) rot=(0,0,1;0rad)
  Support = -> [XY_Plane026]
  sketch-geometry (1):
    g0: Circle CenterX=0 CenterY=0 CenterZ=0 NormalX=0 NormalY=0 NormalZ=1 AngleXU=0 Radius=1.65
  constraints (3):
    c: PointOnObject(g0,g-2)
    c: Diameter(g0) = 3.3
    c: DistanceY(g0) = 0
FEATURE [PartDesign::Pocket] Pocket039
  BaseFeature = -> BaseBend
  Direction = (0,0,-1)
  Length = 5
  Length2 = 5
  Profile = -> Sketch080
  ReferenceAxis = -> Sketch080 [N_Axis]
  Reversed = true
  Type = 1
FEATURE [Sketcher::SketchObject] Sketch081
  FullyConstrained = true
  MapMode = 5
  Support = -> [XY_Plane026]
  sketch-geometry (3):
    g0: ArcOfCircle CenterX=4.5 CenterY=12 CenterZ=0 NormalX=0 NormalY=0 NormalZ=1 AngleXU=0 Radius=3 StartAngle=1e-16 EndAngle=1.57079
    g1: LineSegment StartX=4.50001 StartY=15 StartZ=0 EndX=7.5 EndY=15 EndZ=0
    g2: LineSegment StartX=7.5 StartY=12 StartZ=0 EndX=7.5 EndY=15 EndZ=0
  constraints (9):
    c: Diameter(g0) = 6
    c: Coincident(g1,g0)
    c: Tangent(g1,g0)
    c: Coincident(g2,g1)
    c: Vertical(g2)
    c: Horizontal(g1)
    c: DistanceX(g1) = 7.5
    c: DistanceY(g1) = 15
    c: Tangent(g2,g0) = -1.5708
FEATURE [PartDesign::Pocket] Pocket040
  BaseFeature = -> Pocket039
  Direction = (0,0,-1)
  Length = 5
  Length2 = 5
  Midplane = true
  Profile = -> Sketch081
  ReferenceAxis = -> Sketch081 [N_Axis]
  Type = 1
FEATURE [PartDesign::Mirrored] Mirrored028
  BaseFeature = -> Pocket040
  MirrorPlane = -> Sketch081 [V_Axis]
  Originals = -> [Pocket040]
FEATURE [PartDesign::Body] Body001003005003012
  Group = -> [Sketch078,Sketch079,BaseBend,Sketch080,Pocket039,Sketch081,Pocket040,Mirrored028]
  Origin = -> Origin025
  Tip = -> Mirrored028
COMPONENT P9 — recipe-attached ("plexiglass_holder_top", modeled in this document).
Construction recipe (the document's own serialized feature program — sketch geometry with constraints, then the solid features built on it; lengths are millimeters unless a unit is written):

FEATURE [Sketcher::SketchObject] Sketch082
  FullyConstrained = false
  MapMode = 5
  Support = -> [XY_Plane027]
  sketch-geometry (19):
    g0: ArcOfCircle CenterX=0 CenterY=0 CenterZ=0 NormalX=0 NormalY=0 NormalZ=1 AngleXU=0 Radius=196.875 StartAngle=0.650114 EndAngle=1.5708
    g1: LineSegment StartX=1.21e-14 StartY=196.875 StartZ=0 EndX=1.11e-14 EndY=181.875 EndZ=0
    g2: ArcOfCircle CenterX=0 CenterY=0 CenterZ=0 NormalX=0 NormalY=0 NormalZ=1 AngleXU=0 Radius=181.875 StartAngle=0.650114 EndAngle=1.5708
    g3: ArcOfCircle CenterX=150.746 CenterY=114.625 CenterZ=0 NormalX=0 NormalY=0 NormalZ=1 AngleXU=0 Radius=7.5 StartAngle=3.79171 EndAngle=6.9333
    g4: LineSegment StartX=0 StartY=0 StartZ=0 EndX=164.625 EndY=95.0465 EndZ=0
    g5: GeomPoint X=155.166 Y=108.566 Z=0
    g6: LineSegment StartX=164.625 StartY=95.0465 StartZ=0 EndX=155.166 EndY=108.566 EndZ=0
    g7: ArcOfCircle CenterX=0 CenterY=0 CenterZ=0 NormalX=0 NormalY=0 NormalZ=1 AngleXU=0 Radius=189.375 StartAngle=0.610508 EndAngle=1.5708
    g8: ArcOfCircle CenterX=0 CenterY=0 CenterZ=0 NormalX=0 NormalY=0 NormalZ=1 AngleXU=0 Radius=189.375 StartAngle=0.645052 EndAngle=1.5708
    g9: ArcOfCircle CenterX=0 CenterY=0 CenterZ=0 NormalX=0 NormalY=0 NormalZ=1 AngleXU=0 Radius=196.875 StartAngle=0.612741 EndAngle=0.650114
    g10: LineSegment StartX=155.166 StartY=108.566 StartZ=0 EndX=160.741 EndY=111.784 EndZ=0
    g11: ArcOfCircle CenterX=160.241 CenterY=112.65 CenterZ=0 NormalX=0 NormalY=0 NormalZ=1 AngleXU=0 Radius=1 StartAngle=5.23599 EndAngle=6.89593
    g12: ArcOfCircle CenterX=0 CenterY=0 CenterZ=0 NormalX=0 NormalY=0 NormalZ=1 AngleXU=0 Radius=181.875 StartAngle=0.619097 EndAngle=0.650114
    g13: LineSegment StartX=155.166 StartY=108.566 StartZ=0 EndX=149.434 EndY=105.257 EndZ=0
    g14: ArcOfCircle CenterX=148.934 CenterY=106.123 CenterZ=0 NormalX=0 NormalY=0 NormalZ=1 AngleXU=0 Radius=1 StartAngle=3.76069 EndAngle=5.23599
    g15: ArcOfCircle CenterX=0 CenterY=0 CenterZ=0 NormalX=0 NormalY=0 NormalZ=1 AngleXU=0 Radius=196.875 StartAngle=0.597316 EndAngle=1.5708
    g16: LineSegment StartX=162.786 StartY=110.728 StartZ=0 EndX=0 EndY=0 EndZ=0
    g17: LineSegment StartX=162.786 StartY=110.728 StartZ=0 EndX=0 EndY=110.728 EndZ=0
    g18: LineSegment StartX=0 StartY=0 StartZ=0 EndX=162.786 EndY=110.728 EndZ=0
  constraints (52):
    c: Coincident(g0,g-1)
    c: PointOnObject(g0,g-2)
    c: DistanceY(g0) = 196.875
    c: Coincident(g1,g0)
    c: PointOnObject(g1,g-2)
    c: Coincident(g2,g0)
    c: Coincident(g2,g1)
    c: Tangent(g3,g0) = -1.5708
    c: Tangent(g3,g2) = 1.5708
    c: DistanceY(g1,g1) = 15
    c: Coincident(g4,g0)
    c: Angle(g-1,g4) = 0.523599
    c: PointOnObject(g5,g3)
    c: Coincident(g6,g4)
    c: Coincident(g6,g5)
    c: Coincident(g7,g0)
    c: Coincident(g7,g5)
    c: PointOnObject(g7,g1)
    c: PointOnObject(g3,g7)
    c: Tangent(g6,g7)
    c: Distance(g6) = 16.5
    c: Coincident(g8,g0)
    c: PointOnObject(g8,g-2)
    c: DistanceY(g8,g0) = 7.5
    c: Coincident(g9,g0)
    c: Coincident(g9,g0)
    c: Coincident(g10,g5)
    c: Parallel(g10,g4)
    c: Tangent(g9,g11) = -1.5708
    c: Tangent(g10,g11) = -1.5708
    c: Diameter(g11) = 2
    c: Coincident(g12,g0)
    c: Coincident(g12,g2)
    c: Coincident(g13,g10)
    c: Parallel(g13,g10)
    c: Tangent(g12,g14) = 1.5708
    c: Tangent(g13,g14) = 1.5708
    c: Equal(g14,g11)
    c: Coincident(g15,g0)
    c: PointOnObject(g15,g-2)
    c: Equal(g15,g9)
    c: Distance(g15,g4) = 14.5
    c: Coincident(g16,g15)
    c: Coincident(g16,g0)
    c: Angle(g16,g-2) = 0.97348
    c: Coincident(g17,g15)
    c: PointOnObject(g17,g-2)
    c: Horizontal(g17)
    c: DistanceX(g17,g17) = 162.786
    c: Coincident(g18,g0)
    c: Coincident(g18,g15)
    c: Angle(g16,g-2) = 0.97348
FEATURE [PartDesign::Pad] Pad021
  Direction = (0,0,1)
  Length = 3
  Length2 = 10
  Profile = -> Sketch082
  ReferenceAxis = -> Sketch082 [N_Axis]
  Type = 0
FEATURE [Sketcher::SketchObject] Sketch083
  FullyConstrained = true
  MapMode = 5
  Support = -> [XY_Plane027]
  sketch-geometry (11):
    g0: ArcOfCircle CenterX=0 CenterY=0 CenterZ=0 NormalX=0 NormalY=0 NormalZ=1 AngleXU=0 Radius=196.875 StartAngle=0.650114 EndAngle=1.5708
    g1: LineSegment StartX=1.21e-14 StartY=196.875 StartZ=0 EndX=1.11e-14 EndY=181.875 EndZ=0
    g2: ArcOfCircle CenterX=0 CenterY=0 CenterZ=0 NormalX=0 NormalY=0 NormalZ=1 AngleXU=0 Radius=181.875 StartAngle=0.650114 EndAngle=1.5708
    g3: ArcOfCircle CenterX=150.746 CenterY=114.625 CenterZ=0 NormalX=0 NormalY=0 NormalZ=1 AngleXU=0 Radius=7.5 StartAngle=3.79171 EndAngle=6.9333
    g4: LineSegment StartX=0 StartY=0 StartZ=0 EndX=164.625 EndY=95.0465 EndZ=0
    g5: GeomPoint X=155.166 Y=108.566 Z=0
    g6: LineSegment StartX=164.625 StartY=95.0465 StartZ=0 EndX=155.166 EndY=108.566 EndZ=0
    g7: ArcOfCircle CenterX=0 CenterY=0 CenterZ=0 NormalX=0 NormalY=0 NormalZ=1 AngleXU=0 Radius=189.375 StartAngle=0.610508 EndAngle=1.5708
    g8: ArcOfCircle CenterX=0 CenterY=0 CenterZ=0 NormalX=0 NormalY=0 NormalZ=1 AngleXU=0 Radius=189.375 StartAngle=0.663319 EndAngle=1.5708
    g9: Circle CenterX=149.219 CenterY=116.605 CenterZ=0 NormalX=0 NormalY=0 NormalZ=1 AngleXU=0 Radius=1.7
    g10: Circle CenterX=-149.219 CenterY=116.605 CenterZ=0 NormalX=0 NormalY=0 NormalZ=1 AngleXU=0 Radius=1.7
  constraints (29):
    c: Coincident(g0,g-1)
    c: PointOnObject(g0,g-2)
    c: DistanceY(g0) = 196.875
    c: Coincident(g1,g0)
    c: PointOnObject(g1,g-2)
    c: Coincident(g2,g0)
    c: Coincident(g2,g1)
    c: Tangent(g3,g0) = -1.5708
    c: Tangent(g3,g2) = 1.5708
    c: DistanceY(g1,g1) = 15
    c: Coincident(g4,g0)
    c: Angle(g-1,g4) = 0.523599
    c: PointOnObject(g5,g3)
    c: Coincident(g6,g4)
    c: Coincident(g6,g5)
    c: Coincident(g7,g0)
    c: Coincident(g7,g5)
    c: PointOnObject(g7,g1)
    c: PointOnObject(g3,g7)
    c: Tangent(g6,g7)
    c: Distance(g6) = 16.5
    c: Coincident(g8,g0)
    c: PointOnObject(g8,g-2)
    c: DistanceY(g8,g0) = 7.5
    c: Coincident(g9,g8)
    c: Diameter(g9) = 3.4
    c: Symmetric(g10,g9,g-2)
    c: Equal(g10,g9)
    c: Distance(g5,g9) = 10
FEATURE [PartDesign::Mirrored] Mirrored029
  BaseFeature = -> Pad021
  MirrorPlane = -> Sketch082 [V_Axis]
  Originals = -> [Pad021]
  Refine = true
FEATURE [PartDesign::Pocket] Pocket041
  BaseFeature = -> Mirrored029
  Direction = (0,0,-1)
  Length = 5
  Length2 = 5
  Midplane = true
  Profile = -> Sketch083
  ReferenceAxis = -> Sketch083 [N_Axis]
  Type = 1
FEATURE [Sketcher::SketchObject] Sketch084
  FullyConstrained = true
  MapMode = 5
  Support = -> [XY_Plane027]
  sketch-geometry (15):
    g0: ArcOfCircle CenterX=0 CenterY=0 CenterZ=0 NormalX=0 NormalY=0 NormalZ=1 AngleXU=0 Radius=196.875 StartAngle=0.650114 EndAngle=1.5708
    g1: LineSegment StartX=1.21e-14 StartY=196.875 StartZ=0 EndX=1.11e-14 EndY=181.875 EndZ=0
    g2: ArcOfCircle CenterX=0 CenterY=0 CenterZ=0 NormalX=0 NormalY=0 NormalZ=1 AngleXU=0 Radius=181.875 StartAngle=0.650114 EndAngle=1.5708
    g3: ArcOfCircle CenterX=150.746 CenterY=114.625 CenterZ=0 NormalX=0 NormalY=0 NormalZ=1 AngleXU=0 Radius=7.5 StartAngle=3.79171 EndAngle=6.9333
    g4: LineSegment StartX=0 StartY=0 StartZ=0 EndX=164.625 EndY=95.0465 EndZ=0
    g5: GeomPoint X=155.166 Y=108.566 Z=0
    g6: LineSegment StartX=164.625 StartY=95.0465 StartZ=0 EndX=155.166 EndY=108.566 EndZ=0
    g7: ArcOfCircle CenterX=0 CenterY=0 CenterZ=0 NormalX=0 NormalY=0 NormalZ=1 AngleXU=0 Radius=189.375 StartAngle=0.610508 EndAngle=1.5708
    g8: ArcOfCircle CenterX=0 CenterY=0 CenterZ=0 NormalX=0 NormalY=0 NormalZ=1 AngleXU=0 Radius=196.875 StartAngle=0.612741 EndAngle=0.650114
    g9: LineSegment StartX=155.166 StartY=108.566 StartZ=0 EndX=160.741 EndY=111.784 EndZ=0
    g10: ArcOfCircle CenterX=160.241 CenterY=112.65 CenterZ=0 NormalX=0 NormalY=0 NormalZ=1 AngleXU=0 Radius=1 StartAngle=5.23599 EndAngle=6.89593
    g11: ArcOfCircle CenterX=0 CenterY=0 CenterZ=0 NormalX=0 NormalY=0 NormalZ=1 AngleXU=0 Radius=181.875 StartAngle=0.619097 EndAngle=0.650114
    g12: LineSegment StartX=155.166 StartY=108.566 StartZ=0 EndX=149.434 EndY=105.257 EndZ=0
    g13: ArcOfCircle CenterX=148.934 CenterY=106.123 CenterZ=0 NormalX=0 NormalY=0 NormalZ=1 AngleXU=0 Radius=1 StartAngle=3.76069 EndAngle=5.23599
    g14: Circle CenterX=1.16e-14 CenterY=189.375 CenterZ=0 NormalX=0 NormalY=0 NormalZ=1 AngleXU=0 Radius=1.7
  constraints (37):
    c: Coincident(g0,g-1)
    c: PointOnObject(g0,g-2)
    c: DistanceY(g0) = 196.875
    c: Coincident(g1,g0)
    c: PointOnObject(g1,g-2)
    c: Coincident(g2,g0)
    c: Coincident(g2,g1)
    c: Tangent(g3,g0) = -1.5708
    c: Tangent(g3,g2) = 1.5708
    c: DistanceY(g1,g1) = 15
    c: Coincident(g4,g0)
    c: Angle(g-1,g4) = 0.523599
    c: PointOnObject(g5,g3)
    c: Coincident(g6,g4)
    c: Coincident(g6,g5)
    c: Coincident(g7,g0)
    c: Coincident(g7,g5)
    c: PointOnObject(g7,g1)
    c: PointOnObject(g3,g7)
    c: Tangent(g6,g7)
    c: Distance(g6) = 16.5
    c: Coincident(g8,g0)
    c: Coincident(g8,g0)
    c: Coincident(g9,g5)
    c: Parallel(g9,g4)
    c: Tangent(g8,g10) = -1.5708
    c: Tangent(g9,g10) = -1.5708
    c: Diameter(g10) = 2
    c: Coincident(g11,g0)
    c: Coincident(g11,g2)
    c: Coincident(g12,g9)
    c: Parallel(g12,g9)
    c: Tangent(g11,g13) = 1.5708
    c: Tangent(g12,g13) = 1.5708
    c: Equal(g13,g10)
    c: Coincident(g14,g7)
    c: Diameter(g14) = 3.4
FEATURE [PartDesign::Pocket] Pocket042
  BaseFeature = -> Pocket041
  Direction = (0,0,-1)
  Length = 5
  Length2 = 5
  Midplane = true
  Profile = -> Sketch084
  ReferenceAxis = -> Sketch084 [N_Axis]
  Type = 1
FEATURE [PartDesign::Body] Body001003005003013  label="plexiglass_holder_top"
  Group = -> [Sketch082,Pad021,Sketch083,Mirrored029,Pocket041,Sketch084,Pocket042]
  Origin = -> Origin026
  Placement = pos=(0,0,0) rot=(0,0,1;1.0472rad)
  Tip = -> Pocket042
COMPONENT P10 — recipe-attached ("basin_cover_back_material_0.30ansi", modeled in this document).
Construction recipe (the document's own serialized feature program — sketch geometry with constraints, then the solid features built on it; lengths are millimeters unless a unit is written):

FEATURE [PartDesign::SubShapeBinder] Binder020
  BindCopyOnChange = 0
  BindMode = 0
  ClaimChildren = false
  Context = -> Body001003005003014 [Binder020.]
  Fuse = false
  MakeFace = true
  OffsetFill = false
  OffsetIntersection = false
  OffsetJoinType = 0
  OffsetOpenResult = false
  PartialLoad = false
  Relative = false
  Support = -> [Body001003005003003[Pocket019.Sketch055.]]
  _Version = 2
FEATURE [PartDesign::SubShapeBinder] Binder021
  BindCopyOnChange = 0
  BindMode = 0
  ClaimChildren = false
  Context = -> Body001003005003014 [Binder021.]
  Fuse = false
  MakeFace = true
  OffsetFill = false
  OffsetIntersection = false
  OffsetJoinType = 0
  OffsetOpenResult = false
  PartialLoad = false
  Relative = false
  Support = -> [Body001003005003004[Pocket018.Sketch054.]]
  _Version = 2
FEATURE [PartDesign::CoordinateSystem] Local_CS027
  AttacherType = Attacher::AttachEngine3D
  MapMode = 5
  Support = -> [XY_Plane028]
FEATURE [PartDesign::CoordinateSystem] Local_CS028
  AttacherType = Attacher::AttachEngine3D
  AttachmentOffset = pos=(0,0,0) rot=(0,0,1;0.523599rad)
  MapMode = 5
  Placement = pos=(0,0,0) rot=(0,0,1;0.523599rad)
  Support = -> [XY_Plane028]
FEATURE [PartDesign::Plane] DatumPlane023
  Length = 81.9615
  MapMode = 5
  Placement = pos=(0,0,0) rot=(0,0,1;0.523599rad)
  ResizeMode = 0
  Support = -> [Local_CS028]
  Width = 81.9615
FEATURE [PartDesign::CoordinateSystem] Local_CS029
  AttacherType = Attacher::AttachEngine3D
  AttachmentOffset = pos=(0,16.7432,0) rot=(0,0,1;0.523599rad)
  MapMode = 5
  Placement = pos=(0,16.7432,0) rot=(0,0,1;0.523599rad)
  Support = -> [XY_Plane028]
FEATURE [PartDesign::Pad] Pad022
  Direction = (0,0,1)
  Length = 3
  Length2 = 10
  Profile = -> Sketch047
  ReferenceAxis = -> Sketch047 [N_Axis]
  Type = 0
FEATURE [PartDesign::Pocket] Pocket045
  BaseFeature = -> Pad022
  Direction = (0,0,-1)
  Length = 5
  Length2 = 5
  Midplane = true
  Profile = -> Binder021
  Type = 1
FEATURE [PartDesign::SubShapeBinder] Binder037
  BindCopyOnChange = 0
  BindMode = 0
  ClaimChildren = false
  Context = -> Body001003005003014 [Binder037.]
  Fuse = false
  MakeFace = true
  OffsetFill = false
  OffsetIntersection = false
  OffsetJoinType = 0
  OffsetOpenResult = false
  PartialLoad = false
  Relative = false
  Support = -> [Body001003005003004[Sketch121.Edge2]]
  _Version = 2
FEATURE [PartDesign::CoordinateSystem] Local_CS040
  AttacherType = Attacher::AttachEngine3D
  AttachmentOffset = pos=(0,0,0) rot=(-0.57735,-0.57735,-0.57735;2.0944rad)
  MapMode = 7
  Placement = pos=(150.91,127.052,0) rot=(0,0,1;2.33398rad)
  Support = -> [Binder037]
FEATURE [PartDesign::SubShapeBinder] Binder038
  BindCopyOnChange = 0
  BindMode = 0
  ClaimChildren = false
  Context = -> Body001003005003014 [Binder038.]
  Fuse = false
  MakeFace = true
  OffsetFill = false
  OffsetIntersection = false
  OffsetJoinType = 0
  OffsetOpenResult = false
  PartialLoad = false
  Placement = pos=(150.91,127.052,0) rot=(0,0,1;2.33398rad)
  Relative = true
  Support = -> [tech_pillar[Pocket071.Sketch117.]]
  _Version = 2
FEATURE [PartDesign::Pocket] Pocket059
  BaseFeature = -> Pocket045
  Direction = (0,0,-1)
  Length = 5
  Length2 = 5
  Midplane = true
  Profile = -> Binder038
  Type = 1
FEATURE [PartDesign::SubShapeBinder] Binder047
  BindCopyOnChange = 0
  BindMode = 0
  ClaimChildren = false
  Context = -> Body001003005003014 [Binder047.]
  Fuse = false
  MakeFace = true
  OffsetFill = false
  OffsetIntersection = false
  OffsetJoinType = 0
  OffsetOpenResult = false
  PartialLoad = false
  Placement = pos=(104.99,73.8951,1.5) rot=(0,0,1;0.523599rad)
  Relative = false
  Support = -> [Body001[Sketch073.]]
  _Version = 2
FEATURE [PartDesign::CoordinateSystem] Local_CS045
  AttacherType = Attacher::AttachEngine3D
  AttachmentOffset = pos=(119.5,-3,1.5) rot=(0,0,1;0rad)
  MapMode = 5
  Placement = pos=(104.99,73.8951,1.5) rot=(0,0,1;0.523599rad)
  Support = -> [Local_CS029]
FEATURE [PartDesign::Hole] Hole001
  BaseFeature = -> Pocket059
  CustomThreadClearance = 0
  Depth = 25
  DepthType = 0
  Diameter = 6.5
  DrillForDepth = false
  DrillPoint = 1
  DrillPointAngle = 118
  HoleCutCountersinkAngle = 90
  HoleCutCustomValues = false
  HoleCutDepth = 0
  HoleCutDiameter = 6.1
  HoleCutType = 0
  ModelThread = false
  Profile = -> Binder047
  Reversed = true
  Tapered = false
  TaperedAngle = 90
  ThreadClass = 0
  ThreadDepth = 25
  ThreadDepthType = 0
  ThreadDirection = 0
  ThreadFit = 0
  ThreadSize = 0
  ThreadType = 0
  Threaded = false
  UseCustomThreadClearance = false
FEATURE [PartDesign::Mirrored] Mirrored031
  BaseFeature = -> Hole001
  MirrorPlane = -> Sketch047 [V_Axis]
  Originals = -> [Pad022,Pocket045,Pocket059,Hole001]
  Refine = true
FEATURE [PartDesign::Body] Body001003005003014  label="basin_cover_back_material_0.30ansi"
  Group = -> [Pad022,Binder021,Binder020,Pocket045,Pocket059,Hole001,Mirrored031,Local_CS027,Local_CS028,DatumPlane023,Local_CS029,Binder037,Local_CS040,Binder038,Binder047,Local_CS045]
  Origin = -> Origin027
  Tip = -> Mirrored031
COMPONENT P11 — recipe-attached ("corner_72x15_material_0.30ansi", modeled in this document).
Construction recipe (the document's own serialized feature program — sketch geometry with constraints, then the solid features built on it; lengths are millimeters unless a unit is written):

FEATURE [Sketcher::SketchObject] Sketch085
  FullyConstrained = true
  MapMode = 5
  Placement = pos=(0,0,0) rot=(0.57735,0.57735,0.57735;2.0944rad)
  Support = -> [YZ_Plane028]
  sketch-geometry (2):
    g0: LineSegment StartX=0 StartY=23 StartZ=0 EndX=0 EndY=0 EndZ=0
    g1: LineSegment StartX=0 StartY=0 StartZ=0 EndX=23 EndY=0 EndZ=0
  constraints (6):
    c: PointOnObject(g0,g-2)
    c: Coincident(g0,g-1)
    c: Coincident(g1,g0)
    c: PointOnObject(g1,g-1)
    c: Equal(g1,g0)
    c: DistanceX(g1,g1) = 23  'length'
FEATURE [PartDesign::FeaturePython] BaseBend002  # WARN: FeaturePython — macro-defined, semantics opaque (R4)
  BendSide = 0
  BendSketch = -> Sketch085
  MidPlane = true
  Reverse = false
  length = 86
  radius = 2
  thickness = 0.5
FEATURE [Sketcher::SketchObject] Sketch086
  AttachmentOffset = pos=(43,23,0) rot=(0,0,1;0rad)
  FullyConstrained = true
  MapMode = 5
  Placement = pos=(43,23,0) rot=(0,0,1;0rad)
  Support = -> [XY_Plane029]
  sketch-geometry (3):
    g0: ArcOfCircle CenterX=-7.5 CenterY=-7.5 CenterZ=0 NormalX=0 NormalY=0 NormalZ=1 AngleXU=0 Radius=7.5 StartAngle=0 EndAngle=1.5708
    g1: LineSegment StartX=0 StartY=-7.5 StartZ=0 EndX=0 EndY=0 EndZ=0
    g2: LineSegment StartX=0 StartY=0 StartZ=0 EndX=-7.50003 EndY=-6.21876e-11 EndZ=0
  constraints (8):
    c: PointOnObject(g0,g-2)
    c: PointOnObject(g0,g-1)
    c: Coincident(g1,g-1)
    c: Coincident(g2,g1)
    c: Coincident(g2,g0)
    c: Tangent(g2,g0)
    c: Tangent(g1,g0) = -1.5708
    c: Diameter(g0) = 15
FEATURE [PartDesign::Pocket] Pocket047
  BaseFeature = -> BaseBend002
  Direction = (0,0,-1)
  Length = 5
  Length2 = 5
  Midplane = true
  Profile = -> Sketch086
  ReferenceAxis = -> Sketch086 [N_Axis]
  Type = 1
FEATURE [PartDesign::Mirrored] Mirrored032
  MirrorPlane = -> YZ_Plane028
FEATURE [PartDesign::PolarPattern] PolarPattern010
  Angle = 90
  Axis = -> X_Axis028
  Occurrences = 2
FEATURE [PartDesign::MultiTransform] MultiTransform011
  BaseFeature = -> Pocket047
  Originals = -> [Pocket047]
  Transformations = -> [Mirrored032,PolarPattern010]
FEATURE [Sketcher::SketchObject] Sketch087
  AttachmentOffset = pos=(0,14.5,0) rot=(0,0,1;0rad)
  FullyConstrained = true
  MapMode = 5
  Placement = pos=(0,14.5,0) rot=(0,0,1;0rad)
  Support = -> [XY_Plane029]
  sketch-geometry (2):
    g0: Circle CenterX=36 CenterY=0 CenterZ=0 NormalX=0 NormalY=0 NormalZ=1 AngleXU=0 Radius=1.7
    g1: Circle CenterX=-36 CenterY=0 CenterZ=0 NormalX=0 NormalY=0 NormalZ=1 AngleXU=0 Radius=1.7
  constraints (5):
    c: PointOnObject(g0,g-1)
    c: Symmetric(g1,g0,g-1)
    c: Equal(g0,g1)
    c: Diameter(g0) = 3.4
    c: DistanceX(g1,g0) = 72
FEATURE [PartDesign::Pocket] Pocket048
  BaseFeature = -> MultiTransform011
  Direction = (0,0,-1)
  Length = 5
  Length2 = 5
  Midplane = true
  Profile = -> Sketch087
  ReferenceAxis = -> Sketch087 [N_Axis]
  Type = 1
FEATURE [PartDesign::PolarPattern] PolarPattern011
  Angle = 90
  Axis = -> X_Axis028
  BaseFeature = -> Pocket048
  Occurrences = 2
  Originals = -> [Pocket048]
FEATURE [PartDesign::CoordinateSystem] Local_CS031
  AttacherType = Attacher::AttachEngine3D
  MapMode = 2
  Placement = pos=(0,14.5,0) rot=(0,0,1;0rad)
  Support = -> [Sketch087]
FEATURE [PartDesign::Body] Body001003005003015  label="corner_72x15_material_0.30ansi"
  Group = -> [Sketch085,BaseBend002,Sketch086,Pocket047,MultiTransform011,Mirrored032,PolarPattern010,Sketch087,Pocket048,PolarPattern011,Local_CS031]
  Origin = -> Origin028
  Tip = -> PolarPattern011
COMPONENT P12 — recipe-attached ("corner_5.5_material_0.30ansi", modeled in this document).
Construction recipe (the document's own serialized feature program — sketch geometry with constraints, then the solid features built on it; lengths are millimeters unless a unit is written):

FEATURE [PartDesign::Mirrored] Mirrored039
  MirrorPlane = -> YZ_Plane036
FEATURE [PartDesign::PolarPattern] PolarPattern014
  Angle = 90
  Axis = -> X_Axis036
  Occurrences = 2
FEATURE [Sketcher::SketchObject] Sketch108
  FullyConstrained = true
  MapMode = 5
  Placement = pos=(0,0,0) rot=(0.57735,0.57735,0.57735;2.0944rad)
  Support = -> [YZ_Plane036]
  sketch-geometry (2):
    g0: LineSegment StartX=0 StartY=23 StartZ=0 EndX=0 EndY=0 EndZ=0
    g1: LineSegment StartX=0 StartY=0 StartZ=0 EndX=23 EndY=0 EndZ=0
  constraints (6):
    c: PointOnObject(g0,g-2)
    c: Coincident(g0,g-1)
    c: Coincident(g1,g0)
    c: PointOnObject(g1,g-1)
    c: Equal(g1,g0)
    c: DistanceX(g1,g1) = 23  'length'
FEATURE [PartDesign::FeaturePython] BaseBend007  # WARN: FeaturePython — macro-defined, semantics opaque (R4)
  BendSide = 0
  BendSketch = -> Sketch108
  MidPlane = true
  Reverse = false
  length = 86
  radius = 2
  thickness = 0.5
FEATURE [Sketcher::SketchObject] Sketch109
  AttachmentOffset = pos=(43,23,0) rot=(0,0,1;0rad)
  FullyConstrained = true
  MapMode = 5
  Placement = pos=(43,23,0) rot=(0,0,1;0rad)
  Support = -> [XY_Plane037]
  sketch-geometry (3):
    g0: ArcOfCircle CenterX=-7.5 CenterY=-7.5 CenterZ=0 NormalX=0 NormalY=0 NormalZ=1 AngleXU=0 Radius=7.5 StartAngle=0 EndAngle=1.5708
    g1: LineSegment StartX=0 StartY=-7.5 StartZ=0 EndX=0 EndY=0 EndZ=0
    g2: LineSegment StartX=0 StartY=0 StartZ=0 EndX=-7.50003 EndY=-6.21876e-11 EndZ=0
  constraints (8):
    c: PointOnObject(g0,g-2)
    c: PointOnObject(g0,g-1)
    c: Coincident(g1,g-1)
    c: Coincident(g2,g1)
    c: Coincident(g2,g0)
    c: Tangent(g2,g0)
    c: Tangent(g1,g0) = -1.5708
    c: Diameter(g0) = 15
FEATURE [PartDesign::Pocket] Pocket063
  BaseFeature = -> BaseBend007
  Direction = (0,0,-1)
  Length = 5
  Length2 = 5
  Midplane = true
  Profile = -> Sketch109
  ReferenceAxis = -> Sketch109 [N_Axis]
  Type = 1
FEATURE [PartDesign::MultiTransform] MultiTransform013
  BaseFeature = -> Pocket063
  Originals = -> [Pocket063]
  Transformations = -> [Mirrored039,PolarPattern014]
FEATURE [Sketcher::SketchObject] Sketch110
  AttachmentOffset = pos=(0,14.5,0) rot=(0,0,1;0rad)
  FullyConstrained = true
  MapMode = 5
  Placement = pos=(0,-3.2e-15,14.5) rot=(1,0,0;1.5708rad)
  Support = -> [XZ_Plane036]
  sketch-geometry (2):
    g0: Circle CenterX=36 CenterY=0 CenterZ=0 NormalX=0 NormalY=0 NormalZ=1 AngleXU=0 Radius=1.7
    g1: Circle CenterX=-36 CenterY=0 CenterZ=0 NormalX=0 NormalY=0 NormalZ=1 AngleXU=0 Radius=1.7
  constraints (5):
    c: PointOnObject(g0,g-1)
    c: Symmetric(g1,g0,g-1)
    c: Equal(g0,g1)
    c: Diameter(g0) = 3.4
    c: DistanceX(g1,g0) = 72
FEATURE [PartDesign::CoordinateSystem] Local_CS034
  AttacherType = Attacher::AttachEngine3D
  MapMode = 2
  Placement = pos=(0,-3.2e-15,14.5) rot=(1,0,0;1.5708rad)
  Support = -> [Sketch110]
FEATURE [PartDesign::Pocket] Pocket064
  BaseFeature = -> MultiTransform013
  Direction = (0,1,2e-16)
  Length = 5
  Length2 = 5
  Midplane = true
  Profile = -> Sketch110
  ReferenceAxis = -> Sketch110 [N_Axis]
  Type = 1
FEATURE [Sketcher::SketchObject] Sketch111
  AttachmentOffset = pos=(0,14.5,0) rot=(0,0,1;0rad)
  FullyConstrained = true
  MapMode = 5
  Placement = pos=(0,14.5,0) rot=(0,0,1;0rad)
  Support = -> [XY_Plane037]
  sketch-geometry (2):
    g0: Circle CenterX=36 CenterY=0 CenterZ=0 NormalX=0 NormalY=0 NormalZ=1 AngleXU=0 Radius=2.75
    g1: Circle CenterX=-36 CenterY=0 CenterZ=0 NormalX=0 NormalY=0 NormalZ=1 AngleXU=0 Radius=2.75
  constraints (5):
    c: PointOnObject(g0,g-1)
    c: Symmetric(g1,g0,g-1)
    c: Equal(g0,g1)
    c: Diameter(g0) = 5.5
    c: DistanceX(g1,g0) = 72
FEATURE [PartDesign::Pocket] Pocket065
  BaseFeature = -> Pocket064
  Direction = (0,0,-1)
  Length = 5
  Length2 = 5
  Midplane = true
  Profile = -> Sketch111
  ReferenceAxis = -> Sketch111 [N_Axis]
  Type = 1
FEATURE [PartDesign::Body] Body001003005003015002  label="corner_5.5_material_0.30ansi"
  Group = -> [Sketch108,BaseBend007,Sketch109,Pocket063,MultiTransform013,Mirrored039,PolarPattern014,Sketch110,Pocket064,Local_CS034,Sketch111,Pocket065]
  Origin = -> Origin036
  Tip = -> Pocket065
COMPONENT P13 — recipe-attached ("Body001003005003015005", modeled in this document).
Construction recipe (the document's own serialized feature program — sketch geometry with constraints, then the solid features built on it; lengths are millimeters unless a unit is written):

FEATURE [Sketcher::SketchObject] Sketch131
  FullyConstrained = true
  MapMode = 5
  Support = -> [XY_Plane042]
  sketch-geometry (5):
    g0: LineSegment StartX=-20 StartY=20 StartZ=0 EndX=-20 EndY=0 EndZ=0
    g1: LineSegment StartX=-20 StartY=0 StartZ=0 EndX=20 EndY=0 EndZ=0
    g2: LineSegment StartX=20 StartY=0 StartZ=0 EndX=20 EndY=20 EndZ=0
    g3: LineSegment StartX=20 StartY=20 StartZ=0 EndX=-20 EndY=20 EndZ=0
    g4: GeomPoint X=0 Y=10 Z=0
  constraints (13):
    c: Coincident(g0,g1)
    c: Coincident(g1,g2)
    c: Coincident(g2,g3)
    c: Coincident(g3,g0)
    c: Horizontal(g1)
    c: Horizontal(g3)
    c: Vertical(g0)
    c: Vertical(g2)
    c: Symmetric(g1,g0,g4)
    c: PointOnObject(g4,g-2)
    c: PointOnObject(g1,g-1)
    c: DistanceX(g1,g1) = 40
    c: DistanceY(g2) = 20
FEATURE [PartDesign::Pad] Pad029
  Direction = (0,0,1)
  Length = 1.5
  Length2 = 10
  Profile = -> Sketch131
  ReferenceAxis = -> Sketch131 [N_Axis]
  Type = 0
FEATURE [PartDesign::Body] Body001003005003015005
  Group = -> [Sketch131,Pad029]
  Origin = -> Origin041
  Tip = -> Pad029
COMPONENT P14 — recipe-attached ("top_material_0.50ansi", modeled in this document).
Construction recipe (the document's own serialized feature program — sketch geometry with constraints, then the solid features built on it; lengths are millimeters unless a unit is written):

FEATURE [PartDesign::CoordinateSystem] LCS_0
  AttacherType = Attacher::AttachEngine3D
  MapMode = 2
  Support = -> [X_Axis029]
FEATURE [Sketcher::SketchObject] Sketch089
  FullyConstrained = true
  MapMode = 5
  Placement = pos=(0,0,0) rot=(1,0,0;1.5708rad)
  Support = -> [XZ_Plane029]
  sketch-geometry (5):
    g0: LineSegment StartX=-41.5 StartY=-36.5 StartZ=0 EndX=-41.5 EndY=0 EndZ=0
    g1: LineSegment StartX=-41.5 StartY=0 StartZ=0 EndX=41.5 EndY=0 EndZ=0
    g2: LineSegment StartX=41.5 StartY=0 StartZ=0 EndX=41.5 EndY=-36.5 EndZ=0
    g3: LineSegment StartX=41.5 StartY=-36.5 StartZ=0 EndX=-41.5 EndY=-36.5 EndZ=0
    g4: GeomPoint X=0 Y=-18.25 Z=0
  constraints (13):
    c: Coincident(g0,g1)
    c: Coincident(g1,g2)
    c: Coincident(g2,g3)
    c: Coincident(g3,g0)
    c: Horizontal(g1)
    c: Horizontal(g3)
    c: Vertical(g0)
    c: Vertical(g2)
    c: Symmetric(g1,g0,g4)
    c: PointOnObject(g4,g-2)
    c: PointOnObject(g1,g-1)
    c: DistanceX(g1,g1) = 83  'width'
    c: DistanceY(g2,g2) = 36.5
FEATURE [PartDesign::FeaturePython] BaseBend003  # WARN: FeaturePython — macro-defined, semantics opaque (R4)
  BendSide = 0
  BendSketch = -> Sketch089
  MidPlane = true
  Reverse = false
  length = 108.4
  radius = 0.01
  thickness = 0.3
FEATURE [Sketcher::SketchObject] Sketch090
  FullyConstrained = true
  MapMode = 5
  Support = -> [XY_Plane030]
  sketch-geometry (6):
    g0: LineSegment StartX=0 StartY=-100 StartZ=0 EndX=13 EndY=-100 EndZ=0
    g1: LineSegment StartX=14.5 StartY=-98.5 StartZ=0 EndX=14.5 EndY=100 EndZ=0
    g2: LineSegment StartX=14.5 StartY=100 StartZ=0 EndX=0 EndY=108.372 EndZ=0
    g3: LineSegment StartX=0 StartY=108.372 StartZ=0 EndX=0 EndY=-100 EndZ=0
    g4: ArcOfCircle CenterX=13 CenterY=-98.5 CenterZ=0 NormalX=0 NormalY=0 NormalZ=1 AngleXU=0 Radius=1.5 StartAngle=4.71239 EndAngle=6.28319
    g5: GeomPoint X=14.5 Y=-100 Z=0
  constraints (15):
    c: Coincident(g1,g2)
    c: Coincident(g2,g3)
    c: Coincident(g3,g0)
    c: Horizontal(g0)
    c: Vertical(g3)
    c: PointOnObject(g0,g-2)
    c: DistanceX(g5) = 14.5
    c: Angle(g-2,g2) = 1.0472
    c: Symmetric(g1,g5,g-1)
    c: DistanceY(g5,g1) = 200
    c: PointOnObject(g5,g0)
    c: PointOnObject(g5,g1)
    c: Tangent(g0,g4) = -1.5708
    c: Tangent(g1,g4) = -1.5708
    c: Diameter(g4) = 3
FEATURE [PartDesign::Pad] Pad023
  BaseFeature = -> BaseBend003
  Direction = (0,0,1)
  Length = 0.3
  Length2 = 10
  Profile = -> Sketch090
  ReferenceAxis = -> Sketch090 [N_Axis]
  Reversed = true
  Type = 0
FEATURE [PartDesign::Mirrored] Mirrored034
  BaseFeature = -> Pad023
  MirrorPlane = -> Sketch090 [V_Axis]
  Originals = -> [Pad023]
  Refine = true
FEATURE [Sketcher::SketchObject] Sketch091
  FullyConstrained = true
  MapMode = 5
  Placement = pos=(0,0,0) rot=(0.57735,0.57735,0.57735;2.0944rad)
  Support = -> [YZ_Plane029]
  sketch-geometry (8):
    g0: LineSegment StartX=0 StartY=-36.5 StartZ=0 EndX=0 EndY=-18.63 EndZ=0
    g1: LineSegment StartX=0 StartY=-18.63 StartZ=0 EndX=17.4865 EndY=-18.63 EndZ=0
    g2: LineSegment StartX=54.2 StartY=-36.5 StartZ=0 EndX=54.2 EndY=-18.63 EndZ=0
    g3: ArcOfCircle CenterX=36.33 CenterY=-18.63 CenterZ=0 NormalX=0 NormalY=0 NormalZ=1 AngleXU=0 Radius=17.87 StartAngle=4.71239 EndAngle=6.28319
    g4: LineSegment StartX=54.2 StartY=-36.5 StartZ=0 EndX=36.33 EndY=-36.5 EndZ=0
    g5: ArcOfCircle CenterX=36.33 CenterY=-18.63 CenterZ=0 NormalX=0 NormalY=0 NormalZ=1 AngleXU=0 Radius=17.87 StartAngle=3.19461 EndAngle=4.71239
    g6: ArcOfCircle CenterX=17.4865 CenterY=-19.63 CenterZ=0 NormalX=0 NormalY=0 NormalZ=1 AngleXU=0 Radius=1 StartAngle=0.053019 EndAngle=1.5708
    g7: LineSegment StartX=0 StartY=-36.5 StartZ=0 EndX=36.33 EndY=-36.5 EndZ=0
  constraints (22):
    c: PointOnObject(g0,g-2)
    c: PointOnObject(g0,g-2)
    c: Coincident(g0,g1)
    c: Horizontal(g1)
    c: Vertical(g2)
    c: Coincident(g4,g2)
    c: Horizontal(g4)
    c: Tangent(g3,g2) = -1.5708
    c: Coincident(g5,g3)
    c: Coincident(g5,g3)
    c: Tangent(g1,g6) = 1.5708
    c: Tangent(g6,g5) = 1.5708
    c: Coincident(g7,g0)
    c: Coincident(g7,g3)
    c: Horizontal(g7)
    c: Coincident(g3,g4)
    c: Tangent(g5,g7)
    c: DistanceY(g0) = -36.5
    c: DistanceX(g2) = 54.2
    c: Diameter(g6) = 2
    c: Diameter(g5) = 35.74
    c: Horizontal(g0,g2)
FEATURE [PartDesign::Pocket] Pocket050
  BaseFeature = -> Mirrored034
  Direction = (-1,2e-16,-3e-16)
  Length = 5
  Length2 = 5
  Midplane = true
  Profile = -> Sketch091
  ReferenceAxis = -> Sketch091 [N_Axis]
  Refine = true
  Type = 1
FEATURE [PartDesign::Mirrored] Mirrored035
  BaseFeature = -> Pocket050
  MirrorPlane = -> Sketch091 [V_Axis]
  Originals = -> [Pocket050]
FEATURE [Sketcher::SketchObject] Sketch092
  FullyConstrained = true
  MapMode = 5
  Placement = pos=(0,0,0) rot=(0.57735,0.57735,0.57735;2.0944rad)
  Support = -> [YZ_Plane029]
  sketch-geometry (1):
    g0: Circle CenterX=0 CenterY=-9.63 CenterZ=0 NormalX=0 NormalY=0 NormalZ=1 AngleXU=0 Radius=1.65
  constraints (3):
    c: PointOnObject(g0,g-2)
    c: Diameter(g0) = 3.3
    c: DistanceY(g0) = -9.63
FEATURE [PartDesign::Pocket] Pocket051
  BaseFeature = -> Mirrored035
  Direction = (-1,2e-16,-3e-16)
  Length = 5
  Length2 = 5
  Midplane = true
  Profile = -> Sketch092
  ReferenceAxis = -> Sketch092 [N_Axis]
  Type = 1
FEATURE [PartDesign::Body] Body_2  label="top_material_0.50ansi"
  Group = -> [LCS_0,Sketch089,BaseBend003,Sketch090,Pad023,Mirrored034,Sketch091,Pocket050,Mirrored035,Sketch092,Pocket051]
  Origin = -> Origin029
  Placement = pos=(0,0,3) rot=(0,0,1;0rad)
  Tip = -> Pocket051
COMPONENT P15 — recipe-attached ("vodostok_s_material_0.30ansi", modeled in this document).
Construction recipe (the document's own serialized feature program — sketch geometry with constraints, then the solid features built on it; lengths are millimeters unless a unit is written):

FEATURE [PartDesign::CoordinateSystem] LCS_0002
  AttacherType = Attacher::AttachEngine3D
  MapMode = 2
  Support = -> [X_Axis032]
FEATURE [Sketcher::SketchObject] Sketch094
  FullyConstrained = true
  MapMode = 5
  Support = -> [XY_Plane033]
  sketch-geometry (3):
    g0: Circle CenterX=-86 CenterY=2e-16 CenterZ=0 NormalX=0 NormalY=0 NormalZ=1 AngleXU=0 Radius=1.7
    g1: Circle CenterX=86 CenterY=0 CenterZ=0 NormalX=0 NormalY=0 NormalZ=1 AngleXU=0 Radius=1.7
    g2: Circle CenterX=86 CenterY=-45 CenterZ=0 NormalX=0 NormalY=0 NormalZ=1 AngleXU=0 Radius=1.7
  constraints (8):
    c: PointOnObject(g1,g-1)
    c: Vertical(g2,g1)
    c: Symmetric(g0,g1,g-2)
    c: Equal(g0,g1)
    c: Equal(g1,g2)
    c: Diameter(g1) = 3.4
    c: DistanceX(g0,g1) = 172
    c: DistanceY(g2,g1) = 45
FEATURE [Sketcher::SketchObject] Sketch095
  FullyConstrained = true
  MapMode = 5
  Support = -> [XY_Plane033]
  sketch-geometry (31):
    g0: LineSegment StartX=96 StartY=-87.0059 StartZ=0 EndX=96 EndY=5 EndZ=0
    g1: LineSegment StartX=91 StartY=10 StartZ=0 EndX=-91 EndY=10 EndZ=0
    g2: LineSegment StartX=-96 StartY=5 StartZ=0 EndX=-96 EndY=-5 EndZ=0
    g3: LineSegment StartX=-91 StartY=-10 StartZ=0 EndX=-77 EndY=-10 EndZ=0
    g4: LineSegment StartX=-72 StartY=-15 StartZ=0 EndX=-72 EndY=-59.848 EndZ=0
    g5: LineSegment StartX=-48.163 StartY=-99.1271 StartZ=0 EndX=88.7532 EndY=-94.5016 EndZ=0
    g6: ArcOfCircle CenterX=91 CenterY=5 CenterZ=0 NormalX=0 NormalY=0 NormalZ=1 AngleXU=0 Radius=5 StartAngle=0 EndAngle=1.5708
    g7: GeomPoint X=96 Y=10 Z=0
    g8: ArcOfCircle CenterX=-91 CenterY=-5 CenterZ=0 NormalX=0 NormalY=0 NormalZ=1 AngleXU=0 Radius=5 StartAngle=3.14159 EndAngle=4.71239
    g9: GeomPoint X=-96 Y=-10 Z=0
    g10: ArcOfCircle CenterX=-91 CenterY=5 CenterZ=0 NormalX=0 NormalY=0 NormalZ=1 AngleXU=0 Radius=5 StartAngle=1.5708 EndAngle=3.14159
    g11: GeomPoint X=-96 Y=10 Z=0
    g12: ArcOfCircle CenterX=-77 CenterY=-15 CenterZ=0 NormalX=0 NormalY=0 NormalZ=1 AngleXU=0 Radius=5 StartAngle=0 EndAngle=1.5708
    g13: GeomPoint X=-72 Y=-10 Z=0
    g14: GeomPoint X=-72 Y=-99.9324 Z=0
    g15: ArcOfCircle CenterX=88.5 CenterY=-87.0059 CenterZ=0 NormalX=0 NormalY=0 NormalZ=1 AngleXU=0 Radius=7.5 StartAngle=4.74616 EndAngle=6.28319
    g16: GeomPoint X=96 Y=-94.2568 Z=0
    g17: LineSegment StartX=-72 StartY=-59.9324 StartZ=0 EndX=96 EndY=-54.2568 EndZ=0
    g18: LineSegment StartX=-91 StartY=5 StartZ=0 EndX=-91 EndY=0 EndZ=0
    g19: LineSegment StartX=-91 StartY=0 StartZ=0 EndX=-91 EndY=-5 EndZ=0
    g20: GeomPoint X=86 Y=0 Z=0
    g21: GeomPoint X=-86 Y=0 Z=0
    g22: GeomPoint X=74 Y=0 Z=0
    g23: GeomPoint X=-74 Y=0 Z=0
    g24: LineSegment StartX=-91 StartY=-5 StartZ=0 EndX=-86 EndY=0 EndZ=0
    g25: GeomPoint X=-74 Y=-60 Z=0
    g26: GeomPoint X=74 Y=-55 Z=0
    g27: LineSegment StartX=-71.9971 StartY=-60.0168 StartZ=0 EndX=-71.4099 EndY=-77.3997 EndZ=0
    g28: ArcOfCircle CenterX=-48.9227 CenterY=-76.64 CenterZ=0 NormalX=0 NormalY=0 NormalZ=1 AngleXU=0 Radius=22.5 StartAngle=3.17536 EndAngle=4.74616
    g29: ArcOfCircle CenterX=-67 CenterY=-59.848 CenterZ=0 NormalX=0 NormalY=0 NormalZ=1 AngleXU=0 Radius=5 StartAngle=3.14159 EndAngle=3.17536
    g30: GeomPoint X=-72 Y=-59.9324 Z=0
  constraints (69):
    c: Vertical(g0)
    c: Horizontal(g1)
    c: Vertical(g2)
    c: Horizontal(g3)
    c: Vertical(g4)
    c: PointOnObject(g7,g1)
    c: PointOnObject(g7,g0)
    c: Tangent(g1,g6) = -1.5708
    c: Tangent(g0,g6) = -1.5708
    c: PointOnObject(g9,g3)
    c: PointOnObject(g9,g2)
    c: Tangent(g3,g8) = -1.5708
    c: Tangent(g2,g8) = -1.5708
    c: PointOnObject(g11,g2)
    c: PointOnObject(g11,g1)
    c: Tangent(g2,g10) = -1.5708
    c: Tangent(g1,g10) = -1.5708
    c: PointOnObject(g13,g3)
    c: PointOnObject(g13,g4)
    c: Tangent(g3,g12) = 1.5708
    c: Tangent(g4,g12) = 1.5708
    c: PointOnObject(g14,g4)
    c: PointOnObject(g14,g5)
    c: PointOnObject(g16,g5)
    c: PointOnObject(g16,g0)
    c: Tangent(g5,g15) = -1.5708
    c: Tangent(g0,g15) = -1.5708
    c: Parallel(g17,g5)
    c: Equal(g12,g8)
    c: Equal(g8,g10)
    c: Equal(g10,g6)
    c: Diameter(g10) = 10
    c: Diameter(g15) = 15
    c: Coincident(g18,g10)
    c: PointOnObject(g18,g-1)
    c: Vertical(g18)
    c: Coincident(g18,g19)
    c: Coincident(g19,g8)
    c: Equal(g19,g18)
    c: PointOnObject(g20,g-1)
    c: PointOnObject(g22,g-1)
    c: Symmetric(g21,g20,g-2)
    c: Symmetric(g23,g22,g-2)
    c: DistanceX(g21,g20) = 172
    c: DistanceX(g23,g22) = 148
    c: DistanceY(g9,g11) = 20
    c: Coincident(g24,g8)
    c: Coincident(g24,g21)
    c: Angle(g24,g-1) = 2.35619
    c: DistanceY(g16,g17) = 40
    c: DistanceX(g22,g0) = 22
    c: Vertical(g22,g26)
    c: Vertical(g25,g23)
    c: DistanceY(g25,g26) = 5
    c: PointOnObject(g26,g17)
    c: PointOnObject(g25,g17)
    c: DistanceY(g26,g22) = 55
    c: Coincident(g30,g17)
    c: Perpendicular(g27,g17)
    c: Tangent(g28,g5) = -1.5708
    c: Tangent(g28,g27) = -1.5708
    c: PointOnObject(g17,g0)
    c: Diameter(g28) = 45
    c: DistanceX(g23,g13) = 2
    c: PointOnObject(g30,g27)
    c: PointOnObject(g30,g4)
    c: Tangent(g27,g29) = -1.5708
    c: Tangent(g4,g29) = -1.5708
    c: Diameter(g29) = 10
FEATURE [PartDesign::Pad] Pad025
  Direction = (0,0,1)
  Length = 0.5
  Length2 = 10
  Profile = -> Sketch095
  ReferenceAxis = -> Sketch095 [N_Axis]
  Type = 0
FEATURE [Sketcher::SketchObject] Sketch096
  AttachmentOffset = pos=(0,0,0.5) rot=(0,0,1;0rad)
  FullyConstrained = false
  MapMode = 5
  Placement = pos=(0,0,0.5) rot=(0,0,1;0rad)
  Support = -> [XY_Plane033]
  sketch-geometry (5):
    g0: GeomPoint X=-74 Y=0 Z=0
    g1: GeomPoint X=74 Y=0 Z=0
    g2: GeomPoint X=74 Y=-58 Z=0
    g3: GeomPoint X=-74 Y=-63 Z=0
    g4: LineSegment StartX=-105.813 StartY=-64.0748 StartZ=0 EndX=129.863 EndY=-56.1127 EndZ=0
  constraints (9):
    c: PointOnObject(g1,g-1)
    c: DistanceY(g3,g2) = 5
    c: DistanceY(g2,g1) = 58
    c: Symmetric(g0,g1,g-1)
    c: DistanceX(g0,g1) = 148
    c: Vertical(g2,g1)
    c: Vertical(g3,g0)
    c: PointOnObject(g2,g4)
    c: PointOnObject(g3,g4)
FEATURE [Sketcher::SketchObject] Sketch097
  FullyConstrained = false
  MapMode = 5
  Support = -> [XY_Plane033]
  sketch-geometry (1):
    g0: Circle CenterX=-66 CenterY=-66.2266 CenterZ=0 NormalX=0 NormalY=0 NormalZ=1 AngleXU=0 Radius=2.5
  constraints (2):
    c: Diameter(g0) = 5
    c: DistanceX(g0) = -66
FEATURE [PartDesign::Pocket] Pocket054
  BaseFeature = -> Pad025
  Direction = (0,0,-1)
  Length = 5
  Length2 = 5
  Midplane = true
  Profile = -> Sketch097
  ReferenceAxis = -> Sketch097 [N_Axis]
  Type = 1
FEATURE [PartDesign::Pocket] Pocket055
  BaseFeature = -> Pocket054
  Direction = (0,0,-1)
  Length = 5
  Length2 = 5
  Midplane = true
  Profile = -> Sketch094
  ReferenceAxis = -> Sketch094 [N_Axis]
  Type = 1
FEATURE [PartDesign::FeaturePython] Fold009  # WARN: FeaturePython — macro-defined, semantics opaque (R4)
  BaseFeature = -> Pocket055
  BendLine = -> Sketch096
  Position = 0
  angle = 105
  baseObject = -> Pocket055 [Face5]
  invert = false
  invertbend = false
  kfactor = 0.5
  radius = 2
  unfold = false
FEATURE [PartDesign::Body] Body_4  label="vodostok_s_material_0.30ansi"
  Group = -> [LCS_0002,Sketch094,Sketch095,Pad025,Sketch096,Sketch097,Pocket054,Pocket055,Fold009]
  Origin = -> Origin032
  Tip = -> Fold009
COMPONENT P16 — recipe-attached ("plexiglass_holder_bottom_tech", modeled in this document).
Construction recipe (the document's own serialized feature program — sketch geometry with constraints, then the solid features built on it; lengths are millimeters unless a unit is written):

FEATURE [PartDesign::CoordinateSystem] LCS_0004
  AttacherType = Attacher::AttachEngine3D
  MapMode = 2
  Support = -> [X_Axis034]
FEATURE [Sketcher::SketchObject] Sketch101
  FullyConstrained = false
  MapMode = 5
  Support = -> [XY_Plane035]
  sketch-geometry (12):
    g0: LineSegment StartX=1.06e-14 StartY=173.684 StartZ=0 EndX=1.21e-14 EndY=196.875 EndZ=0
    g1: LineSegment StartX=0 StartY=0 StartZ=0 EndX=170.499 EndY=98.4377 EndZ=0
    g2: ArcOfCircle CenterX=0 CenterY=0 CenterZ=0 NormalX=0 NormalY=0 NormalZ=1 AngleXU=0 Radius=173.684 StartAngle=0.625357 EndAngle=1.5708
    g3: ArcOfCircle CenterX=0 CenterY=0 CenterZ=0 NormalX=0 NormalY=0 NormalZ=1 AngleXU=0 Radius=196.875 StartAngle=0.763183 EndAngle=1.5708
    g4: LineSegment StartX=142.27 StartY=136.085 StartZ=0 EndX=150.91 EndY=127.052 EndZ=0
    g5: LineSegment StartX=150.91 StartY=127.052 StartZ=0 EndX=159.551 EndY=118.019 EndZ=0
    g6: LineSegment StartX=146.574 StartY=122.905 StartZ=0 EndX=150.91 EndY=127.052 EndZ=0
    g7: LineSegment StartX=150.91 StartY=127.052 StartZ=0 EndX=158.859 EndY=118.742 EndZ=0
    g8: ArcOfCircle CenterX=158.137 CenterY=118.051 CenterZ=0 NormalX=0 NormalY=0 NormalZ=1 AngleXU=0 Radius=1 StartAngle=5.47557 EndAngle=7.04637
    g9: LineSegment StartX=158.828 StartY=117.328 StartZ=0 EndX=142.317 EndY=101.535 EndZ=0
    g10: ArcOfCircle CenterX=141.626 CenterY=102.258 CenterZ=0 NormalX=0 NormalY=0 NormalZ=1 AngleXU=0 Radius=1 StartAngle=3.76695 EndAngle=5.47557
    g11: GeomPoint X=141.485 Y=100.739 Z=0
  constraints (31):
    c: PointOnObject(g0,g-2)
    c: PointOnObject(g0,g-2)
    c: Coincident(g2,g0)
    c: Coincident(g3,g0)
    c: Angle(g-1,g1) = 0.523599
    c: DistanceY(g0) = 196.875  'r'
    c: Coincident(g2,g-1)
    c: Coincident(g2,g1)
    c: Coincident(g5,g4)
    c: Parallel(g4,g5)
    c: Equal(g4,g5)
    c: Tangent(g4,g3) = 1.5708
    c: Coincident(g6,g4)
    c: Perpendicular(g6,g4)
    c: Distance(g5,g3) = 25
    c: Coincident(g3,g2)
    c: Coincident(g7,g4)
    c: PointOnObject(g7,g5)
    c: PointOnObject(g5,g9)
    c: Tangent(g9,g8) = 1.5708
    c: Perpendicular(g5,g9)
    c: Tangent(g10,g9) = 1.5708
    c: Tangent(g10,g2) = 1.5708
    c: Equal(g10,g8)
    c: Diameter(g10) = 2
    c: Tangent(g8,g7) = 1.5708
    c: PointOnObject(g11,g9)
    c: PointOnObject(g11,g2)
    c: Distance(g11,g5) = 25
    c: DistanceY(g0,g0) = 23.1913
    c: Distance(g6) = 6
FEATURE [PartDesign::Pad] Pad026
  Direction = (0,0,1)
  Length = 3
  Length2 = 10
  Profile = -> Sketch101
  ReferenceAxis = -> Sketch101 [N_Axis]
  Type = 0
FEATURE [PartDesign::SubShapeBinder] Binder039
  BindCopyOnChange = 0
  BindMode = 0
  ClaimChildren = false
  Context = -> Body_6 [Binder039.]
  Fuse = false
  MakeFace = true
  OffsetFill = false
  OffsetIntersection = false
  OffsetJoinType = 0
  OffsetOpenResult = false
  PartialLoad = false
  Relative = true
  Support = -> [Body001003005003014[Binder038.]]
  _Version = 2
FEATURE [PartDesign::Pocket] Pocket058
  BaseFeature = -> Pad026
  Direction = (0,0,-1)
  Length = 5
  Length2 = 5
  Midplane = true
  Profile = -> Binder039
  Type = 1
FEATURE [PartDesign::Mirrored] Mirrored037
  BaseFeature = -> Pocket058
  MirrorPlane = -> Sketch101 [V_Axis]
  Originals = -> [Pad026,Pocket058]
  Refine = true
FEATURE [PartDesign::SubShapeBinder] Binder040
  BindCopyOnChange = 0
  BindMode = 0
  ClaimChildren = false
  Context = -> Body_6 [Binder040.]
  Fuse = false
  MakeFace = true
  OffsetFill = false
  OffsetIntersection = false
  OffsetJoinType = 0
  OffsetOpenResult = false
  PartialLoad = false
  Placement = pos=(0,196.875,0) rot=(0,0,1;3.14159rad)
  Relative = true
  Support = -> [tech_mid[Pocket076.Sketch123.]]
  _Version = 2
FEATURE [PartDesign::Pocket] Pocket078
  BaseFeature = -> Mirrored037
  Direction = (0,0,-1)
  Length = 5
  Length2 = 5
  Midplane = true
  Profile = -> Binder040
  Type = 1
FEATURE [PartDesign::Body] Body_6  label="plexiglass_holder_bottom_tech"
  Group = -> [LCS_0004,Sketch101,Pad026,Pocket058,Mirrored037,Binder039,Binder040,Pocket078]
  Origin = -> Origin034
  Tip = -> Pocket078
COMPONENT P17 — recipe-attached ("ugol_mini_material_0.30ansi", modeled in this document).
Construction recipe (the document's own serialized feature program — sketch geometry with constraints, then the solid features built on it; lengths are millimeters unless a unit is written):

FEATURE [PartDesign::CoordinateSystem] LCS_0005
  AttacherType = Attacher::AttachEngine3D
  MapMode = 2
  Support = -> [X_Axis035]
FEATURE [Sketcher::SketchObject] Sketch104
  FullyConstrained = false
  MapMode = 5
  Placement = pos=(0,0,0) rot=(0.57735,0.57735,0.57735;2.0944rad)
  Support = -> [YZ_Plane035]
  sketch-geometry (3):
    g0: LineSegment StartX=10.9 StartY=0 StartZ=0 EndX=0 EndY=0 EndZ=0
    g1: LineSegment StartX=0 StartY=0 StartZ=0 EndX=0 EndY=17.2 EndZ=0
    g2: GeomPoint X=12.5 Y=0 Z=0
  constraints (7):
    c: PointOnObject(g0,g-1)
    c: Coincident(g0,g-1)
    c: Coincident(g0,g1)
    c: PointOnObject(g1,g-2)
    c: PointOnObject(g2,g-1)
    c: DistanceY(g1) = 17.2
    c: DistanceX(g0,g0) = 10.9
FEATURE [PartDesign::FeaturePython] BaseBend006  # WARN: FeaturePython — macro-defined, semantics opaque (R4)
  BendSide = 0
  BendSketch = -> Sketch104
  MidPlane = true
  Reverse = false
  length = 9.4
  radius = 2
  thickness = 0.5
FEATURE [Sketcher::SketchObject] Sketch105
  AttachmentOffset = pos=(0,5.9,0) rot=(0,0,1;0rad)
  FullyConstrained = true
  MapMode = 5
  Placement = pos=(0,5.9,0) rot=(0,0,1;0rad)
  Support = -> [XY_Plane036]
  sketch-geometry (1):
    g0: Circle CenterX=0 CenterY=0 CenterZ=0 NormalX=0 NormalY=0 NormalZ=1 AngleXU=0 Radius=1.7
  constraints (2):
    c: Coincident(g0,g-1)
    c: Diameter(g0) = 3.4
FEATURE [PartDesign::Plane] DatumPlane024
  AttachmentOffset = pos=(0,0,0) rot=(1,0,0;0.785398rad)
  Length = 61.8921
  MapMode = 5
  Placement = pos=(0,0,0) rot=(1,0,0;0.785398rad)
  ResizeMode = 0
  Support = -> [XY_Plane036]
  Width = 82.6027
FEATURE [PartDesign::Fillet] Fillet002
  Base = -> BaseBend006 [Edge25,Edge8]
  BaseFeature = -> BaseBend006
  Radius = 2
  SupportTransform = false
  UseAllEdges = false
FEATURE [PartDesign::Mirrored] Mirrored038
  BaseFeature = -> Fillet002
  MirrorPlane = -> YZ_Plane035
  Originals = -> [Fillet002]
FEATURE [PartDesign::Pocket] Pocket061
  BaseFeature = -> Mirrored038
  Direction = (0,0,-1)
  Length = 5
  Length2 = 5
  Midplane = true
  Profile = -> Sketch105
  ReferenceAxis = -> Sketch105 [N_Axis]
  Type = 1
FEATURE [Sketcher::SketchObject] Sketch106
  AttachmentOffset = pos=(0,12.5,0) rot=(0,0,1;0rad)
  FullyConstrained = true
  MapMode = 5
  Placement = pos=(0,-2.8e-15,12.5) rot=(1,0,0;1.5708rad)
  Support = -> [XZ_Plane035]
  sketch-geometry (1):
    g0: Circle CenterX=0 CenterY=0 CenterZ=0 NormalX=0 NormalY=0 NormalZ=1 AngleXU=0 Radius=1.7
  constraints (2):
    c: Coincident(g0,g-1)
    c: Diameter(g0) = 3.4
FEATURE [PartDesign::Pocket] Pocket062
  BaseFeature = -> Pocket061
  Direction = (0,1,2e-16)
  Length = 5
  Length2 = 5
  Midplane = true
  Profile = -> Sketch106
  ReferenceAxis = -> Sketch106 [N_Axis]
  Type = 1
FEATURE [PartDesign::Body] Body_7  label="ugol_mini_material_0.30ansi"
  Group = -> [LCS_0005,Sketch104,BaseBend006,Sketch105,DatumPlane024,Fillet002,Mirrored038,Pocket061,Sketch106,Pocket062]
  Origin = -> Origin035
  Tip = -> Pocket062
